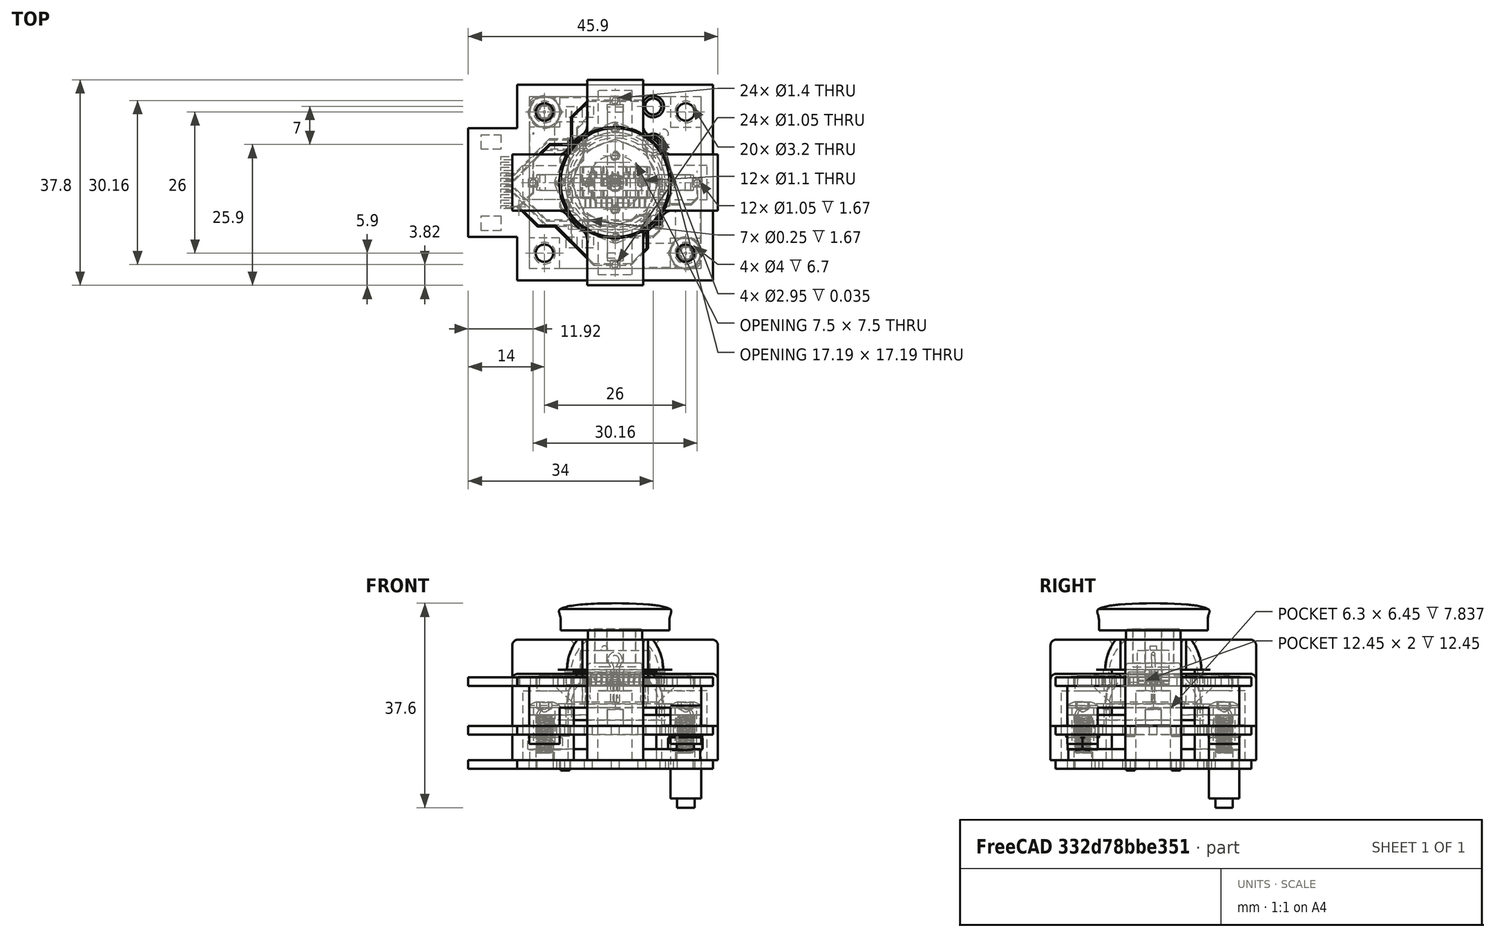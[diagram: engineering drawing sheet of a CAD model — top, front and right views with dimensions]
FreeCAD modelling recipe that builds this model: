
FCSTD DOCUMENT  (FreeCAD 0.21R33771 (Git))
Label: Thumbstick
License: All rights reserved
LicenseURL: http://en.wikipedia.org/wiki/All_rights_reserved
objects: Part::Feature×187, App::Part×27, PartDesign::Body×25, Sketcher::SketchObject×19, PartDesign::FeatureBase×16, PartDesign::ShapeBinder×14, PartDesign::Pad×12, App::DocumentObjectGroupPython×10, PartDesign::Fillet×9, Part::FeaturePython×6, PartDesign::Boolean×5, PartDesign::Pocket×4, PartDesign::SubShapeBinder×4, Mesh::Feature×4, PartDesign::Revolution×3, Spreadsheet::Sheet×1, PartDesign::Chamfer×1, App::DocumentObjectGroup×1
note: 334 computed .brp shape members not serialized (recipe doc carries the construction recipe); baked Part::Feature solids carry a one-line shape summary decoded from their .brp

FEATURE [Spreadsheet::Sheet] Spreadsheet  label="params"
  cells = A2='pcb_board_outline; B2(pcb_board_outline)=36; A3='pcb_mounting_distance; B3(pcb_mounting_distance)=26; A4='pcb_sw_array_len; B4(pcb_sw_array_len)=32.8; A6='sw_x; B6(sw_x)=12.8; A7='sw_y; B7(sw_y)=5.8; A8='sw_z; B8(sw_z)=6.5; A9='sw_to_button_top; B9(sw_to_button_top)=7.35; A10='sw_array_gap; B10(sw_array_gap)=7.2; A11='sw_button_width; B11(sw_button_width)=2.9; A13='post_center_width; B13(post_center_width)=6; A14='post_height; B14(post_height)=10.5; A15='post_tip_height; B15(post_tip_height)=2; A16='arm_height; B16(arm_height)=2; A18='mating_cross_width; B18(mating_cross_width)=7.5; A19='mating_cross_slot_width; B19(mating_cross_slot_width)=3; A20='mating_cross_slot_depth; B20(mating_cross_slot_depth)=7; A22='swivel_shell_thickness; B22(swivel_shell_thickness)=2; A23='ccover_shell_thickness; B23(ccover_shell_thickness)=2; A25='stick_fit_tolerance; B25(stick_fit_tolerance)=0; A26='stick_extrusion_height; B26(stick_extrusion_height)=6; A27='stick_cap_height; B27(stick_cap_height)=5; A29='collar_outer_rim_height; B29(collar_outer_rim_height)=8; A30='collar_inner_rim_height; B30(collar_inner_rim_height)=7; A31='collar_width; B31(collar_width)=8; A32='collar_center_spacing; B32(collar_center_spacing)=15; A34='pcb_thickness; B34(pcb_thickness)=1.6; A35='pcb_clip_extrude; B35(pcb_clip_extrude)=1; A36='pcb_clip_overlang_length; B36(pcb_clip_overlang_length)=2.5; A38='pcb_allign_holes; B38(pcb_allign_holes)=1.6; A39='pcb_mounting_holes; B39(pcb_mounting_holes)=3; A40='pcb_sw_pth; B40(pcb_sw_pth)=1.1; A42='pcb_cover_overhang; B42(pcb_cover_overhang)=0.9; A43='pcb_clip_thickness; B43(pcb_clip_thickness)=1.5; A45='insert_length; B45(insert_length)=5.7; A46='insert_hole_dia; B46(insert_hole_dia)=4; A47='insert_min_wall_thickness; B47(insert_min_wall_thickness)=1.6
FEATURE [Sketcher::SketchObject] Sketch  label="Sketch_Arms"
  FullyConstrained = true
  MapMode = 5
  Support = -> [XY_Plane001]
  expr: Constraints[14] = <<params>>.pcb_sw_array_len - 5
  expr: Constraints[18] = <<params>>.sw_button_width
  sketch-geometry (12):
    g0: LineSegment StartX=-13.9 StartY=1.45 StartZ=0 EndX=-13.9 EndY=-1.45 EndZ=0
    g1: LineSegment StartX=-13.9 StartY=-1.45 StartZ=0 EndX=-1.45 EndY=-1.45 EndZ=0
    g2: LineSegment StartX=-1.45 StartY=-13.9 StartZ=0 EndX=1.45 EndY=-13.9 EndZ=0
    g3: LineSegment StartX=13.9 StartY=-1.45 StartZ=0 EndX=13.9 EndY=1.45 EndZ=0
    g4: LineSegment StartX=13.9 StartY=1.45 StartZ=0 EndX=1.45 EndY=1.45 EndZ=0
    g5: LineSegment StartX=1.45 StartY=1.45 StartZ=0 EndX=1.45 EndY=13.9 EndZ=0
    g6: LineSegment StartX=1.45 StartY=13.9 StartZ=0 EndX=-1.45 EndY=13.9 EndZ=0
    g7: LineSegment StartX=-1.45 StartY=13.9 StartZ=0 EndX=-1.45 EndY=1.45 EndZ=0
    g8: LineSegment StartX=-1.45 StartY=1.45 StartZ=0 EndX=-13.9 EndY=1.45 EndZ=0
    g9: LineSegment StartX=1.45 StartY=-13.9 StartZ=0 EndX=1.45 EndY=-1.45 EndZ=0
    g10: LineSegment StartX=1.45 StartY=-1.45 StartZ=0 EndX=13.9 EndY=-1.45 EndZ=0
    g11: LineSegment StartX=-1.45 StartY=-1.45 StartZ=0 EndX=-1.45 EndY=-13.9 EndZ=0
  constraints (30):
    c: Coincident(g8,g0)
    c: Coincident(g0,g1)
    c: Horizontal(g1)
    c: Coincident(g11,g2)
    c: Coincident(g2,g9)
    c: Coincident(g10,g3)
    c: Coincident(g3,g4)
    c: Coincident(g5,g6)
    c: Coincident(g6,g7)
    c: Symmetric(g11,g2,g-2)
    c: Symmetric(g6,g5,g-2)
    c: Symmetric(g8,g0,g-1)
    c: Symmetric(g3,g10,g-1)
    c: Equal(g6,g0)
    c: DistanceY(g2,g5) = 27.8
    c: Symmetric(g3,g8,g-2)
    c: Symmetric(g5,g2,g-1)
    c: Equal(g5,g4)
    c: DistanceY(g3,g3) = 2.9
    c: Horizontal(g8)
    c: Vertical(g9)
    c: Vertical(g11)
    c: Coincident(g9,g10)
    c: Coincident(g1,g11)
    c: Coincident(g8,g7)
    c: Coincident(g5,g4)
    c: Horizontal(g4)
    c: Vertical(g5)
    c: Horizontal(g10)
    c: Vertical(g7)
FEATURE [Sketcher::SketchObject] Sketch001  label="Sketch_Center"
  FullyConstrained = true
  MapMode = 5
  Placement = pos=(0,0,0) rot=(1,0,0;1.5708rad)
  Support = -> [XZ_Plane002]
  expr: Constraints[10] = <<params>>.sw_array_gap + 1
  expr: Constraints[11] = Spreadsheet.post_height
  expr: Constraints[19] = <<params>>.post_tip_height
  expr: Constraints[9] = <<params>>.arm_height
  sketch-geometry (7):
    g0: LineSegment StartX=8.2 StartY=2 StartZ=0 EndX=8.2 EndY=0 EndZ=0
    g1: LineSegment StartX=8.2 StartY=0 StartZ=0 EndX=0 EndY=0 EndZ=0
    g2: ArcOfCircle CenterX=0 CenterY=2 CenterZ=0 NormalX=0 NormalY=0 NormalZ=1 AngleXU=0 Radius=8.2 StartAngle=0 EndAngle=0.915197
    g3: LineSegment StartX=4.999 StartY=8.5 StartZ=0 EndX=4.999 EndY=10.5 EndZ=0
    g4: LineSegment StartX=4.999 StartY=10.5 StartZ=0 EndX=0 EndY=10.5 EndZ=0
    g5: LineSegment StartX=0 StartY=10.5 StartZ=0 EndX=0 EndY=0 EndZ=0
    g6: LineSegment StartX=8.2 StartY=2 StartZ=0 EndX=0 EndY=2 EndZ=0
  constraints (20):
    c: PointOnObject(g0,g-1)
    c: Vertical(g0)
    c: Coincident(g1,g0)
    c: Coincident(g3,g2)
    c: Vertical(g3)
    c: Coincident(g4,g3)
    c: PointOnObject(g4,g-2)
    c: Horizontal(g4)
    c: Coincident(g5,g4)
    c: DistanceY(g0,g0) = 2
    c: DistanceX(g-1,g0) = 8.2
    c: DistanceY(g-1,g4) = 10.5
    c: Coincident(g1,g-1)
    c: Coincident(g5,g1)
    c: Coincident(g6,g0)
    c: PointOnObject(g6,g5)
    c: Horizontal(g6)
    c: Coincident(g0,g2)
    c: Coincident(g2,g6)
    c: DistanceY(g3,g3) = 2
FEATURE [PartDesign::Revolution] Revolution
  Angle = 360
  Axis = (0,-2e-16,1)
  Base = (0,0,0)
  Placement = pos=(0,0,0) rot=(1,0,0;1.5708rad)
  Profile = -> Sketch001
  ReferenceAxis = -> Sketch001 [V_Axis]
  Reversed = true
FEATURE [PartDesign::Pad] Pad  label="Pad_Arms"
  Direction = (0,0,1)
  Length = 2
  Length2 = 10
  Profile = -> Sketch
  ReferenceAxis = -> Sketch [N_Axis]
  Type = 0
  expr: Length = <<params>>.arm_height
FEATURE [PartDesign::Body] Body  label="Arms"
  Group = -> [Sketch,Pad]
  Origin = -> Origin001
  Tip = -> Pad
FEATURE [PartDesign::Boolean] Boolean
  BaseFeature = -> Revolution
  Group = -> [Body]
  Type = 0
FEATURE [PartDesign::ShapeBinder] ShapeBinder
  Placement = pos=(0,0,0) rot=(1,0,0;1.5708rad)
  Support = -> [Revolution]
  TraceSupport = false
FEATURE [Sketcher::SketchObject] Sketch002  label="Sketch_PocketMatingCross"
  FullyConstrained = true
  MapMode = 5
  Placement = pos=(0,2.3e-15,10.5) rot=(0,0,1;3.14159rad)
  Support = -> [ShapeBinder]
  expr: Constraints[32] = <<params>>.mating_cross_width
  expr: Constraints[33] = <<params>>.mating_cross_slot_width
  sketch-geometry (12):
    g0: LineSegment StartX=-3.75 StartY=1.5 StartZ=0 EndX=-1.5 EndY=1.5 EndZ=0
    g1: LineSegment StartX=-1.5 StartY=3.75 StartZ=0 EndX=-1.5 EndY=1.5 EndZ=0
    g2: LineSegment StartX=-1.5 StartY=3.75 StartZ=0 EndX=1.5 EndY=3.75 EndZ=0
    g3: LineSegment StartX=1.5 StartY=3.75 StartZ=0 EndX=1.5 EndY=1.5 EndZ=0
    g4: LineSegment StartX=1.5 StartY=1.5 StartZ=0 EndX=3.75 EndY=1.5 EndZ=0
    g5: LineSegment StartX=3.75 StartY=1.5 StartZ=0 EndX=3.75 EndY=-1.5 EndZ=0
    g6: LineSegment StartX=3.75 StartY=-1.5 StartZ=0 EndX=1.5 EndY=-1.5 EndZ=0
    g7: LineSegment StartX=1.5 StartY=-1.5 StartZ=0 EndX=1.5 EndY=-3.75 EndZ=0
    g8: LineSegment StartX=1.5 StartY=-3.75 StartZ=0 EndX=-1.5 EndY=-3.75 EndZ=0
    g9: LineSegment StartX=-1.5 StartY=-3.75 StartZ=0 EndX=-1.5 EndY=-1.5 EndZ=0
    g10: LineSegment StartX=-1.5 StartY=-1.5 StartZ=0 EndX=-3.75 EndY=-1.5 EndZ=0
    g11: LineSegment StartX=-3.75 StartY=-1.5 StartZ=0 EndX=-3.75 EndY=1.5 EndZ=0
  constraints (34):
    c: Horizontal(g0)
    c: Coincident(g1,g0)
    c: Vertical(g1)
    c: Coincident(g2,g1)
    c: Horizontal(g2)
    c: Coincident(g3,g2)
    c: Vertical(g3)
    c: Coincident(g4,g3)
    c: Horizontal(g4)
    c: Coincident(g5,g4)
    c: Vertical(g5)
    c: Coincident(g6,g5)
    c: Horizontal(g6)
    c: Coincident(g7,g6)
    c: Coincident(g8,g7)
    c: Horizontal(g8)
    c: Coincident(g9,g8)
    c: Vertical(g9)
    c: Coincident(g10,g9)
    c: Horizontal(g10)
    c: Coincident(g11,g10)
    c: Coincident(g11,g0)
    c: Vertical(g11)
    c: Equal(g11,g5)
    c: Equal(g5,g8)
    c: Equal(g8,g2)
    c: Equal(g3,g7)
    c: Equal(g4,g0)
    c: Equal(g4,g3)
    c: Symmetric(g9,g6,g-2)
    c: Symmetric(g3,g6,g-1)
    c: Vertical(g7)
    c: DistanceX(g0,g4) = 7.5
    c: DistanceX(g2,g2) = 3
FEATURE [PartDesign::Pocket] Pocket  label="Pocket_mating_cross"
  BaseFeature = -> Boolean
  Direction = (0,2e-16,-1)
  Length = 7
  Length2 = 5
  Profile = -> Sketch002
  ReferenceAxis = -> Sketch002 [N_Axis]
  Type = 0
  expr: Length = <<params>>.mating_cross_slot_depth
FEATURE [Part::Feature] Part__Feature  label="Fusion"
  shape: bbox 12.8 x 5.8 x 10.85 mm, 76 faces (baked)
FEATURE [App::Part] Kailh_GM_4_0
  Group = -> [Part__Feature]
  Origin = -> Origin005
  Placement = pos=(10,0,1.65) rot=(0,0,1;3.14159rad)
FEATURE [Part::Feature] Part__Feature001  label="Fusion001"
  shape: bbox 12.8 x 5.8 x 10.85 mm, 76 faces (baked)
FEATURE [App::Part] Kailh_GM_4_001
  Group = -> [Part__Feature001]
  Origin = -> Origin006
  Placement = pos=(0,10,1.65) rot=(0,0,-1;1.5708rad)
FEATURE [Part::Feature] Part__Feature002  label="C_0805_2012Metric"
  shape: bbox 2 x 1.25 x 1.25 mm, 28 faces (baked)
FEATURE [App::Part] C_0805_2012Metric  label="C_0805_2012Metric001"
  Group = -> [Part__Feature002]
  Origin = -> Origin007
  Placement = pos=(-7,7,1.65) rot=(0,0,1;0rad)
FEATURE [Part::Feature] Part__Feature003  label="C_0805_2012Metric002"
  shape: bbox 2 x 1.25 x 1.25 mm, 28 faces (baked)
FEATURE [App::Part] C_0805_2012Metric001  label="C_0805_2012Metric003"
  Group = -> [Part__Feature003]
  Origin = -> Origin008
  Placement = pos=(6.9625,-7,1.65) rot=(0,0,1;0rad)
FEATURE [Part::Feature] Part__Feature004  label="Fusion002"
  shape: bbox 12.8 x 5.8 x 10.85 mm, 76 faces (baked)
FEATURE [App::Part] Kailh_GM_4_002
  Group = -> [Part__Feature004]
  Origin = -> Origin009
  Placement = pos=(-10,0,1.65) rot=(0,0,1;0rad)
FEATURE [Part::Feature] Part__Feature005  label="Fusion003"
  shape: bbox 12.8 x 5.8 x 10.85 mm, 76 faces (baked)
FEATURE [App::Part] Kailh_GM_4_003
  Group = -> [Part__Feature005]
  Origin = -> Origin010
  Placement = pos=(0,-10,1.65) rot=(0,0,1;1.5708rad)
FEATURE [Part::Feature] Part__Feature006  label="TE_1_84952_0"
  shape: bbox 17.92 x 6.54 x 2.56 mm, 212 faces (baked)
FEATURE [App::Part] TE_1_84952_0_1x10_1MP_P1_0mm_Horizontal  label="TE_1-84952-0_1x10-1MP_P1.0mm_Horizontal"
  Group = -> [Part__Feature006]
  Origin = -> Origin011
  Placement = pos=(-21.8,0,-0.05) rot=(0.707107,0.707107,0;3.14159rad)
FEATURE [Part::Feature] Part__Feature007  label="SOT_23_6"
  shape: bbox 2.8 x 2.9 x 1.55 mm, 124 faces (baked)
FEATURE [App::Part] SOT_23_6  label="SOT-23-6"
  Group = -> [Part__Feature007]
  Origin = -> Origin012
  Placement = pos=(-7,7,-0.05) rot=(0,1,0;3.14159rad)
FEATURE [Part::Feature] Part__Feature008  label="SOT_23_007"
  shape: bbox 2.8 x 2.9 x 1.55 mm, 124 faces (baked)
FEATURE [App::Part] SOT_23_007  label="SOT-23-007"
  Group = -> [Part__Feature008]
  Origin = -> Origin013
  Placement = pos=(6.9625,-7,-0.05) rot=(0,1,0;3.14159rad)
FEATURE [Part::Feature] Part__Feature009  label="thumbpad_track_1"
  shape: bbox 0.125 x 0.2 x 0.035 mm, 6 faces (baked)
FEATURE [Part::Feature] Part__Feature010  label="thumbpad_track_2"
  shape: bbox 0.25 x 0.25 x 0.035 mm, 6 faces (baked)
FEATURE [Part::Feature] Part__Feature011  label="thumbpad_track_3"
  shape: bbox 0.2 x 0.2 x 0.035 mm, 6 faces (baked)
FEATURE [Part::Feature] Part__Feature012  label="thumbpad_track_4"
  shape: bbox 6.2 x 0.2 x 0.035 mm, 6 faces (baked)
FEATURE [Part::Feature] Part__Feature013  label="thumbpad_track_5"
  shape: bbox 0.2 x 3.505 x 0.035 mm, 6 faces (baked)
FEATURE [Part::Feature] Part__Feature014  label="thumbpad_track_6"
  shape: bbox 4.505 x 0.2 x 0.035 mm, 6 faces (baked)
FEATURE [Part::Feature] Part__Feature015  label="thumbpad_track_7"
  shape: bbox 0.8002 x 0.8777 x 0.035 mm, 6 faces (baked)
FEATURE [Part::Feature] Part__Feature016  label="thumbpad_track_8"
  shape: bbox 0.2 x 1.442 x 0.035 mm, 7 faces (baked)
FEATURE [Part::Feature] Part__Feature017  label="thumbpad_track_9"
  shape: bbox 3.317 x 3.317 x 0.035 mm, 6 faces (baked)
FEATURE [Part::Feature] Part__Feature018  label="thumbpad_track_10"
  shape: bbox 2.505 x 0.2 x 0.035 mm, 6 faces (baked)
FEATURE [Part::Feature] Part__Feature019  label="thumbpad_track_11"
  shape: bbox 3.205 x 3.205 x 0.035 mm, 6 faces (baked)
FEATURE [Part::Feature] Part__Feature020  label="thumbpad_track_12"
  shape: bbox 1.28 x 1.28 x 0.035 mm, 6 faces (baked)
FEATURE [Part::Feature] Part__Feature021  label="thumbpad_track_13"
  shape: bbox 0.2 x 4.988 x 0.035 mm, 6 faces (baked)
FEATURE [Part::Feature] Part__Feature022  label="thumbpad_track_14"
  shape: bbox 3.988 x 0.2 x 0.035 mm, 6 faces (baked)
FEATURE [Part::Feature] Part__Feature023  label="thumbpad_track_15"
  shape: bbox 0.2 x 5.1 x 0.035 mm, 7 faces (baked)
FEATURE [Part::Feature] Part__Feature024  label="thumbpad_track_16"
  shape: bbox 7.28 x 7.28 x 0.035 mm, 6 faces (baked)
FEATURE [Part::Feature] Part__Feature025  label="thumbpad_track_17"
  shape: bbox 0.2 x 0.95 x 0.035 mm, 6 faces (baked)
FEATURE [Part::Feature] Part__Feature026  label="thumbpad_track_19"
  shape: bbox 3.622 x 3.622 x 0.035 mm, 7 faces (baked)
FEATURE [Part::Feature] Part__Feature027  label="thumbpad_track_20"
  shape: bbox 2.275 x 2.275 x 0.035 mm, 6 faces (baked)
FEATURE [Part::Feature] Part__Feature028  label="thumbpad_track_21"
  shape: bbox 0.2 x 2.505 x 0.035 mm, 7 faces (baked)
FEATURE [Part::Feature] Part__Feature029  label="thumbpad_track_22"
  shape: bbox 4.505 x 0.2 x 0.035 mm, 6 faces (baked)
FEATURE [Part::Feature] Part__Feature030  label="thumbpad_track_23"
  shape: bbox 3.505 x 0.2 x 0.035 mm, 6 faces (baked)
FEATURE [Part::Feature] Part__Feature031  label="thumbpad_track_24"
  shape: bbox 2.755 x 2.755 x 0.035 mm, 6 faces (baked)
FEATURE [Part::Feature] Part__Feature032  label="thumbpad_track_25"
  shape: bbox 3.413 x 0.2 x 0.035 mm, 6 faces (baked)
FEATURE [Part::Feature] Part__Feature033  label="thumbpad_track_26"
  shape: bbox 3.28 x 3.28 x 0.035 mm, 6 faces (baked)
FEATURE [Part::Feature] Part__Feature034  label="thumbpad_track_27"
  shape: bbox 2.314 x 0.2 x 0.035 mm, 6 faces (baked)
FEATURE [Part::Feature] Part__Feature035  label="thumbpad_track_28"
  shape: bbox 0.125 x 0.2 x 0.035 mm, 6 faces (baked)
FEATURE [Part::Feature] Part__Feature036  label="thumbpad_track_30"
  shape: bbox 0.2 x 1.85 x 0.035 mm, 7 faces (baked)
FEATURE [Part::Feature] Part__Feature037  label="thumbpad_track_31"
  shape: bbox 2.075 x 0.2 x 0.035 mm, 6 faces (baked)
FEATURE [Part::Feature] Part__Feature038  label="thumbpad_track_32"
  shape: bbox 6.7 x 6.7 x 0.035 mm, 6 faces (baked)
FEATURE [Part::Feature] Part__Feature039  label="thumbpad_track_33"
  shape: bbox 0.2 x 2.025 x 0.035 mm, 7 faces (baked)
FEATURE [Part::Feature] Part__Feature040  label="thumbpad_track_34"
  shape: bbox 8.025 x 0.2 x 0.035 mm, 6 faces (baked)
FEATURE [Part::Feature] Part__Feature041  label="thumbpad_track_35"
  shape: bbox 1.105 x 0.2 x 0.035 mm, 6 faces (baked)
FEATURE [Part::Feature] Part__Feature042  label="thumbpad_track_36"
  shape: bbox 1.15 x 1.15 x 0.035 mm, 6 faces (baked)
FEATURE [Part::Feature] Part__Feature043  label="thumbpad_track_37"
  shape: bbox 7.62 x 0.2 x 0.035 mm, 6 faces (baked)
FEATURE [Part::Feature] Part__Feature044  label="thumbpad_track_38"
  shape: bbox 6.65 x 6.65 x 0.035 mm, 6 faces (baked)
FEATURE [Part::Feature] Part__Feature045  label="thumbpad_track_39"
  shape: bbox 4.113 x 0.2 x 0.035 mm, 6 faces (baked)
FEATURE [Part::Feature] Part__Feature046  label="thumbpad_track_40"
  shape: bbox 1.7 x 0.2 x 0.035 mm, 6 faces (baked)
FEATURE [Part::Feature] Part__Feature047  label="thumbpad_track_41"
  shape: bbox 0.2 x 5.113 x 0.035 mm, 6 faces (baked)
FEATURE [Part::Feature] Part__Feature048  label="thumbpad_track_42"
  shape: bbox 0.3375 x 0.3375 x 0.035 mm, 6 faces (baked)
FEATURE [Part::Feature] Part__Feature049  label="thumbpad_track_43"
  shape: bbox 2.2 x 2.2 x 0.035 mm, 6 faces (baked)
FEATURE [Part::Feature] Part__Feature050  label="thumbpad_track_44"
  shape: bbox 1.7 x 0.2 x 0.035 mm, 6 faces (baked)
FEATURE [Part::Feature] Part__Feature051  label="thumbpad_track_45"
  shape: bbox 5.013 x 0.2 x 0.035 mm, 6 faces (baked)
FEATURE [Part::Feature] Part__Feature052  label="thumbpad_track_46"
  shape: bbox 5.75 x 5.75 x 0.035 mm, 6 faces (baked)
FEATURE [Part::Feature] Part__Feature053  label="thumbpad_track_47"
  shape: bbox 0.675 x 0.675 x 0.035 mm, 6 faces (baked)
FEATURE [Part::Feature] Part__Feature054  label="thumbpad_track_48"
  shape: bbox 0.2 x 1.2 x 0.035 mm, 6 faces (baked)
FEATURE [Part::Feature] Part__Feature055  label="thumbpad_track_49"
  shape: bbox 0.2 x 3.675 x 0.035 mm, 6 faces (baked)
FEATURE [Part::Feature] Part__Feature056  label="thumbpad_track_50"
  shape: bbox 0.8625 x 0.2 x 0.035 mm, 6 faces (baked)
FEATURE [Part::Feature] Part__Feature057  label="thumbpad_track_51"
  shape: bbox 4.845 x 0.2 x 0.035 mm, 6 faces (baked)
FEATURE [Part::Feature] Part__Feature058  label="thumbpad_track_52"
  shape: bbox 14.03 x 0.2 x 0.035 mm, 6 faces (baked)
FEATURE [Part::Feature] Part__Feature059  label="thumbpad_track_53"
  shape: bbox 1.105 x 0.2 x 0.035 mm, 6 faces (baked)
FEATURE [Part::Feature] Part__Feature060  label="thumbpad_track_54"
  shape: bbox 0.2 x 3.25 x 0.035 mm, 6 faces (baked)
FEATURE [Part::Feature] Part__Feature061  label="thumbpad_track_55"
  shape: bbox 6.65 x 6.65 x 0.035 mm, 6 faces (baked)
FEATURE [Part::Feature] Part__Feature062  label="thumbpad_track_56"
  shape: bbox 3.397 x 0.2 x 0.035 mm, 6 faces (baked)
FEATURE [Part::Feature] Part__Feature063  label="thumbpad_track_57"
  shape: bbox 2.25 x 2.25 x 0.035 mm, 6 faces (baked)
FEATURE [Part::Feature] Part__Feature064  label="thumbpad_track_58"
  shape: bbox 0.2 x 2.113 x 0.035 mm, 6 faces (baked)
FEATURE [Part::Feature] Part__Feature065  label="thumbpad_track_59"
  shape: bbox 3.944 x 3.944 x 0.035 mm, 6 faces (baked)
FEATURE [Part::Feature] Part__Feature066  label="thumbpad_track_60"
  shape: bbox 2.1 x 2.1 x 0.035 mm, 6 faces (baked)
FEATURE [Part::Feature] Part__Feature067  label="thumbpad_track_61"
  shape: bbox 0.2 x 3.735 x 0.035 mm, 7 faces (baked)
FEATURE [Part::Feature] Part__Feature068  label="thumbpad_track_62"
  shape: bbox 1.3 x 1.3 x 0.035 mm, 6 faces (baked)
FEATURE [Part::Feature] Part__Feature069  label="thumbpad_track_63"
  shape: bbox 0.2 x 1.15 x 0.035 mm, 6 faces (baked)
FEATURE [Part::Feature] Part__Feature070  label="thumbpad_track_64"
  shape: bbox 6.585 x 0.2 x 0.035 mm, 6 faces (baked)
FEATURE [Part::Feature] Part__Feature071  label="thumbpad_pad_5"
  shape: bbox 4 x 4 x 0.035 mm, 4 faces (baked)
FEATURE [Part::Feature] Part__Feature072  label="thumbpad_pad_6"
  shape: bbox 4 x 4 x 0.035 mm, 4 faces (baked)
FEATURE [Part::Feature] Part__Feature073  label="thumbpad_pad_7"
  shape: bbox 3 x 3 x 1.67 mm, 4 faces (baked)
FEATURE [Part::Feature] Part__Feature074  label="thumbpad_pad_8"
  shape: bbox 1.7 x 1.7 x 0.035 mm, 7 faces (baked)
FEATURE [Part::Feature] Part__Feature075  label="thumbpad_pad_9"
  shape: bbox 1.7 x 1.7 x 0.035 mm, 7 faces (baked)
FEATURE [Part::Feature] Part__Feature076  label="thumbpad_pad_10"
  shape: bbox 1.1 x 1.1 x 1.67 mm, 4 faces (baked)
FEATURE [Part::Feature] Part__Feature077  label="thumbpad_pad_11"
  shape: bbox 1.7 x 1.7 x 0.035 mm, 4 faces (baked)
FEATURE [Part::Feature] Part__Feature078  label="thumbpad_pad_12"
  shape: bbox 1.7 x 1.7 x 0.035 mm, 4 faces (baked)
FEATURE [Part::Feature] Part__Feature079  label="thumbpad_pad_13"
  shape: bbox 1.1 x 1.1 x 1.67 mm, 4 faces (baked)
FEATURE [Part::Feature] Part__Feature080  label="thumbpad_pad_14"
  shape: bbox 1.7 x 1.7 x 0.035 mm, 4 faces (baked)
FEATURE [Part::Feature] Part__Feature081  label="thumbpad_pad_15"
  shape: bbox 1.7 x 1.7 x 0.035 mm, 4 faces (baked)
FEATURE [Part::Feature] Part__Feature082  label="thumbpad_pad_16"
  shape: bbox 1.1 x 1.1 x 1.67 mm, 4 faces (baked)
FEATURE [Part::Feature] Part__Feature083  label="thumbpad_pad_19"
  shape: bbox 1.7 x 1.7 x 0.035 mm, 7 faces (baked)
FEATURE [Part::Feature] Part__Feature084  label="thumbpad_pad_20"
  shape: bbox 1.7 x 1.7 x 0.035 mm, 7 faces (baked)
FEATURE [Part::Feature] Part__Feature085  label="thumbpad_pad_21"
  shape: bbox 1.1 x 1.1 x 1.67 mm, 4 faces (baked)
FEATURE [Part::Feature] Part__Feature086  label="thumbpad_pad_22"
  shape: bbox 1.7 x 1.7 x 0.035 mm, 4 faces (baked)
FEATURE [Part::Feature] Part__Feature087  label="thumbpad_pad_23"
  shape: bbox 1.7 x 1.7 x 0.035 mm, 4 faces (baked)
FEATURE [Part::Feature] Part__Feature088  label="thumbpad_pad_24"
  shape: bbox 1.1 x 1.1 x 1.67 mm, 4 faces (baked)
FEATURE [Part::Feature] Part__Feature089  label="thumbpad_pad_25"
  shape: bbox 1.7 x 1.7 x 0.035 mm, 4 faces (baked)
FEATURE [Part::Feature] Part__Feature090  label="thumbpad_pad_26"
  shape: bbox 1.7 x 1.7 x 0.035 mm, 4 faces (baked)
FEATURE [Part::Feature] Part__Feature091  label="thumbpad_pad_27"
  shape: bbox 1.1 x 1.1 x 1.67 mm, 4 faces (baked)
FEATURE [Part::Feature] Part__Feature092  label="thumbpad_pad_28"
  shape: bbox 4 x 4 x 0.035 mm, 4 faces (baked)
FEATURE [Part::Feature] Part__Feature093  label="thumbpad_pad_29"
  shape: bbox 4 x 4 x 0.035 mm, 4 faces (baked)
FEATURE [Part::Feature] Part__Feature094  label="thumbpad_pad_30"
  shape: bbox 3 x 3 x 1.67 mm, 4 faces (baked)
FEATURE [Part::Feature] Part__Feature095  label="thumbpad_pad_31"
  shape: bbox 1.175 x 1.45 x 0.035 mm, 23 faces (baked)
FEATURE [Part::Feature] Part__Feature096  label="thumbpad_pad_32"
  shape: bbox 1.175 x 1.45 x 0.035 mm, 23 faces (baked)
FEATURE [Part::Feature] Part__Feature097  label="thumbpad_pad_33"
  shape: bbox 1.175 x 1.45 x 0.035 mm, 23 faces (baked)
FEATURE [Part::Feature] Part__Feature098  label="thumbpad_pad_34"
  shape: bbox 1.175 x 1.45 x 0.035 mm, 23 faces (baked)
FEATURE [Part::Feature] Part__Feature099  label="thumbpad_pad_37"
  shape: bbox 1.7 x 1.7 x 0.035 mm, 7 faces (baked)
FEATURE [Part::Feature] Part__Feature100  label="thumbpad_pad_38"
  shape: bbox 1.7 x 1.7 x 0.035 mm, 7 faces (baked)
FEATURE [Part::Feature] Part__Feature101  label="thumbpad_pad_39"
  shape: bbox 1.1 x 1.1 x 1.67 mm, 4 faces (baked)
FEATURE [Part::Feature] Part__Feature102  label="thumbpad_pad_40"
  shape: bbox 1.7 x 1.7 x 0.035 mm, 4 faces (baked)
FEATURE [Part::Feature] Part__Feature103  label="thumbpad_pad_41"
  shape: bbox 1.7 x 1.7 x 0.035 mm, 4 faces (baked)
FEATURE [Part::Feature] Part__Feature104  label="thumbpad_pad_42"
  shape: bbox 1.1 x 1.1 x 1.67 mm, 4 faces (baked)
FEATURE [Part::Feature] Part__Feature105  label="thumbpad_pad_43"
  shape: bbox 1.7 x 1.7 x 0.035 mm, 4 faces (baked)
FEATURE [Part::Feature] Part__Feature106  label="thumbpad_pad_44"
  shape: bbox 1.7 x 1.7 x 0.035 mm, 4 faces (baked)
FEATURE [Part::Feature] Part__Feature107  label="thumbpad_pad_45"
  shape: bbox 1.1 x 1.1 x 1.67 mm, 4 faces (baked)
FEATURE [Part::Feature] Part__Feature108  label="thumbpad_pad_46"
  shape: bbox 1.7 x 1.7 x 0.035 mm, 7 faces (baked)
FEATURE [Part::Feature] Part__Feature109  label="thumbpad_pad_47"
  shape: bbox 1.7 x 1.7 x 0.035 mm, 7 faces (baked)
FEATURE [Part::Feature] Part__Feature110  label="thumbpad_pad_48"
  shape: bbox 1.1 x 1.1 x 1.67 mm, 4 faces (baked)
FEATURE [Part::Feature] Part__Feature111  label="thumbpad_pad_49"
  shape: bbox 1.7 x 1.7 x 0.035 mm, 4 faces (baked)
FEATURE [Part::Feature] Part__Feature112  label="thumbpad_pad_50"
  shape: bbox 1.7 x 1.7 x 0.035 mm, 4 faces (baked)
FEATURE [Part::Feature] Part__Feature113  label="thumbpad_pad_51"
  shape: bbox 1.1 x 1.1 x 1.67 mm, 4 faces (baked)
FEATURE [Part::Feature] Part__Feature114  label="thumbpad_pad_52"
  shape: bbox 1.7 x 1.7 x 0.035 mm, 4 faces (baked)
FEATURE [Part::Feature] Part__Feature115  label="thumbpad_pad_53"
  shape: bbox 1.7 x 1.7 x 0.035 mm, 4 faces (baked)
FEATURE [Part::Feature] Part__Feature116  label="thumbpad_pad_54"
  shape: bbox 1.1 x 1.1 x 1.67 mm, 4 faces (baked)
FEATURE [Part::Feature] Part__Feature117  label="thumbpad_pad_55"
  shape: bbox 2 x 2 x 0.035 mm, 6 faces (baked)
FEATURE [Part::Feature] Part__Feature118  label="thumbpad_pad_56"
  shape: bbox 2 x 2 x 0.035 mm, 6 faces (baked)
FEATURE [Part::Feature] Part__Feature119  label="thumbpad_pad_57"
  shape: bbox 2 x 0.61 x 0.035 mm, 6 faces (baked)
FEATURE [Part::Feature] Part__Feature120  label="thumbpad_pad_58"
  shape: bbox 2 x 0.61 x 0.035 mm, 6 faces (baked)
FEATURE [Part::Feature] Part__Feature121  label="thumbpad_pad_59"
  shape: bbox 2 x 0.61 x 0.035 mm, 6 faces (baked)
FEATURE [Part::Feature] Part__Feature122  label="thumbpad_pad_60"
  shape: bbox 2 x 0.61 x 0.035 mm, 6 faces (baked)
FEATURE [Part::Feature] Part__Feature123  label="thumbpad_pad_61"
  shape: bbox 2 x 0.61 x 0.035 mm, 6 faces (baked)
FEATURE [Part::Feature] Part__Feature124  label="thumbpad_pad_62"
  shape: bbox 2 x 0.61 x 0.035 mm, 6 faces (baked)
FEATURE [Part::Feature] Part__Feature125  label="thumbpad_pad_63"
  shape: bbox 2 x 0.61 x 0.035 mm, 6 faces (baked)
FEATURE [Part::Feature] Part__Feature126  label="thumbpad_pad_64"
  shape: bbox 2 x 0.61 x 0.035 mm, 6 faces (baked)
FEATURE [Part::Feature] Part__Feature127  label="thumbpad_pad_65"
  shape: bbox 2 x 0.61 x 0.035 mm, 6 faces (baked)
FEATURE [Part::Feature] Part__Feature128  label="thumbpad_pad_66"
  shape: bbox 2 x 0.61 x 0.035 mm, 6 faces (baked)
FEATURE [Part::Feature] Part__Feature129  label="thumbpad_pad_67"
  shape: bbox 3.6 x 2.68 x 0.035 mm, 6 faces (baked)
FEATURE [Part::Feature] Part__Feature130  label="thumbpad_pad_68"
  shape: bbox 3.6 x 2.68 x 0.035 mm, 6 faces (baked)
FEATURE [Part::Feature] Part__Feature131  label="thumbpad_pad_69"
  shape: bbox 1.325 x 0.6 x 0.035 mm, 22 faces (baked)
FEATURE [Part::Feature] Part__Feature132  label="thumbpad_pad_70"
  shape: bbox 1.325 x 0.6 x 0.035 mm, 23 faces (baked)
FEATURE [Part::Feature] Part__Feature133  label="thumbpad_pad_71"
  shape: bbox 1.325 x 0.6 x 0.035 mm, 22 faces (baked)
FEATURE [Part::Feature] Part__Feature134  label="thumbpad_pad_72"
  shape: bbox 1.325 x 0.6 x 0.035 mm, 22 faces (baked)
FEATURE [Part::Feature] Part__Feature135  label="thumbpad_pad_73"
  shape: bbox 1.325 x 0.6 x 0.035 mm, 23 faces (baked)
FEATURE [Part::Feature] Part__Feature136  label="thumbpad_pad_74"
  shape: bbox 1.325 x 0.6 x 0.035 mm, 22 faces (baked)
FEATURE [Part::Feature] Part__Feature137  label="thumbpad_pad_75"
  shape: bbox 2 x 2 x 0.035 mm, 6 faces (baked)
FEATURE [Part::Feature] Part__Feature138  label="thumbpad_pad_76"
  shape: bbox 1.325 x 0.6 x 0.035 mm, 22 faces (baked)
FEATURE [Part::Feature] Part__Feature139  label="thumbpad_pad_77"
  shape: bbox 1.325 x 0.6 x 0.035 mm, 23 faces (baked)
FEATURE [Part::Feature] Part__Feature140  label="thumbpad_pad_78"
  shape: bbox 1.325 x 0.6 x 0.035 mm, 22 faces (baked)
FEATURE [Part::Feature] Part__Feature141  label="thumbpad_pad_79"
  shape: bbox 1.325 x 0.6 x 0.035 mm, 22 faces (baked)
FEATURE [Part::Feature] Part__Feature142  label="thumbpad_pad_80"
  shape: bbox 1.325 x 0.6 x 0.035 mm, 23 faces (baked)
FEATURE [Part::Feature] Part__Feature143  label="thumbpad_pad_81"
  shape: bbox 1.325 x 0.6 x 0.035 mm, 22 faces (baked)
FEATURE [Part::Feature] Part__Feature144  label="thumbpad_pad_82"
  shape: bbox 2 x 2 x 0.035 mm, 6 faces (baked)
FEATURE [Part::Feature] Part__Feature145  label="thumbpad_pad_83"
  shape: bbox 0.6 x 0.6 x 0.035 mm, 4 faces (baked)
FEATURE [Part::Feature] Part__Feature146  label="thumbpad_pad_84"
  shape: bbox 0.6 x 0.6 x 0.035 mm, 4 faces (baked)
FEATURE [Part::Feature] Part__Feature147  label="thumbpad_pad_85"
  shape: bbox 0.3 x 0.3 x 1.67 mm, 4 faces (baked)
FEATURE [Part::Feature] Part__Feature148  label="thumbpad_pad_86"
  shape: bbox 0.6 x 0.6 x 0.035 mm, 4 faces (baked)
FEATURE [Part::Feature] Part__Feature149  label="thumbpad_pad_87"
  shape: bbox 0.6 x 0.6 x 0.035 mm, 4 faces (baked)
FEATURE [Part::Feature] Part__Feature150  label="thumbpad_pad_88"
  shape: bbox 0.3 x 0.3 x 1.67 mm, 4 faces (baked)
FEATURE [Part::Feature] Part__Feature151  label="thumbpad_pad_89"
  shape: bbox 0.6 x 0.6 x 0.035 mm, 4 faces (baked)
FEATURE [Part::Feature] Part__Feature152  label="thumbpad_pad_90"
  shape: bbox 0.6 x 0.6 x 0.035 mm, 4 faces (baked)
FEATURE [Part::Feature] Part__Feature153  label="thumbpad_pad_91"
  shape: bbox 0.3 x 0.3 x 1.67 mm, 4 faces (baked)
FEATURE [Part::Feature] Part__Feature154  label="thumbpad_pad_92"
  shape: bbox 0.6 x 0.6 x 0.035 mm, 4 faces (baked)
FEATURE [Part::Feature] Part__Feature155  label="thumbpad_pad_93"
  shape: bbox 0.6 x 0.6 x 0.035 mm, 4 faces (baked)
FEATURE [Part::Feature] Part__Feature156  label="thumbpad_pad_94"
  shape: bbox 0.3 x 0.3 x 1.67 mm, 4 faces (baked)
FEATURE [Part::Feature] Part__Feature157  label="thumbpad_pad_95"
  shape: bbox 0.6 x 0.6 x 0.035 mm, 4 faces (baked)
FEATURE [Part::Feature] Part__Feature158  label="thumbpad_pad_96"
  shape: bbox 0.6 x 0.6 x 0.035 mm, 4 faces (baked)
FEATURE [Part::Feature] Part__Feature159  label="thumbpad_pad_97"
  shape: bbox 0.3 x 0.3 x 1.67 mm, 4 faces (baked)
FEATURE [Part::Feature] Part__Feature160  label="thumbpad_pad_98"
  shape: bbox 0.6 x 0.6 x 0.035 mm, 4 faces (baked)
FEATURE [Part::Feature] Part__Feature161  label="thumbpad_pad_99"
  shape: bbox 0.6 x 0.6 x 0.035 mm, 4 faces (baked)
FEATURE [Part::Feature] Part__Feature162  label="thumbpad_pad_100"
  shape: bbox 0.3 x 0.3 x 1.67 mm, 4 faces (baked)
FEATURE [Part::Feature] Part__Feature163  label="thumbpad_pad_101"
  shape: bbox 0.6 x 0.6 x 0.035 mm, 4 faces (baked)
FEATURE [Part::Feature] Part__Feature164  label="thumbpad_pad_102"
  shape: bbox 0.6 x 0.6 x 0.035 mm, 4 faces (baked)
FEATURE [Part::Feature] Part__Feature165  label="thumbpad_pad_103"
  shape: bbox 0.3 x 0.3 x 1.67 mm, 4 faces (baked)
FEATURE [Part::Feature] Part__Feature166  label="thumbpad_PCB"
  shape: bbox 45 x 36 x 1.6 mm, 35 faces (baked)
FEATURE [App::Part] thumbpad_1  label="thumbpad_pcb"
  Group = -> [Kailh_GM_4_0,Kailh_GM_4_001,C_0805_2012Metric,C_0805_2012Metric001,Kailh_GM_4_002,Kailh_GM_4_003,TE_1_84952_0_1x10_1MP_P1_0mm_Horizontal,SOT_23_6,SOT_23_007,Part__Feature009,Part__Feature010,Part__Feature011,Part__Feature012,Part__Feature013,Part__Feature014,Part__Feature015,Part__Feature016,Part__Feature017,Part__Feature018,Part__Feature019,Part__Feature020,Part__Feature021,Part__Feature022,+144 more]
  Origin = -> Origin014
  Placement = pos=(0,0,-9) rot=(0,0,1;0rad)
FEATURE [PartDesign::SubShapeBinder] Binder002  label="Binder_MatingCross_surface"
  BindCopyOnChange = 0
  BindMode = 0
  ClaimChildren = false
  Context = -> Part002 [Body003.Binder002.]
  Fuse = false
  MakeFace = true
  OffsetFill = false
  OffsetIntersection = false
  OffsetJoinType = 0
  OffsetOpenResult = false
  PartialLoad = false
  Relative = true
  Support = -> [Part[Body001.Pocket.Face45]]
  _Version = 2
FEATURE [Part::Feature] Part__Feature167  label="Fusion004"
  shape: bbox 12.8 x 5.8 x 10.85 mm, 76 faces (baked)
FEATURE [App::Part] Kailh_GM_4_004
  Group = -> [Part__Feature167]
  Origin = -> Origin024
  Placement = pos=(10,0,1.65) rot=(0,0,1;3.14159rad)
FEATURE [Part::Feature] Part__Feature168  label="Fusion005"
  shape: bbox 12.8 x 5.8 x 10.85 mm, 76 faces (baked)
FEATURE [App::Part] Kailh_GM_4_005
  Group = -> [Part__Feature168]
  Origin = -> Origin025
  Placement = pos=(0,10,1.65) rot=(0,0,-1;1.5708rad)
FEATURE [Part::Feature] Part__Feature171  label="C_0805_2012Metric006"
  shape: bbox 2 x 1.25 x 1.25 mm, 28 faces (baked)
FEATURE [App::Part] C_0805_2012Metric003  label="C_0805_2012Metric007"
  Group = -> [Part__Feature171]
  Origin = -> Origin028
  Placement = pos=(6.9625,-7,1.65) rot=(0,0,1;0rad)
FEATURE [Part::Feature] Part__Feature172  label="Fusion006"
  shape: bbox 12.8 x 5.8 x 10.85 mm, 76 faces (baked)
FEATURE [App::Part] Kailh_GM_4_006
  Group = -> [Part__Feature172]
  Origin = -> Origin029
  Placement = pos=(-10,0,1.65) rot=(0,0,1;0rad)
FEATURE [Part::Feature] Part__Feature173  label="Fusion007"
  shape: bbox 12.8 x 5.8 x 10.85 mm, 76 faces (baked)
FEATURE [App::Part] Kailh_GM_4_007
  Group = -> [Part__Feature173]
  Origin = -> Origin030
  Placement = pos=(0,-10,1.65) rot=(0,0,1;1.5708rad)
FEATURE [Part::Feature] Part__Feature176  label="SOT_23_009"
  shape: bbox 2.8 x 2.9 x 1.55 mm, 124 faces (baked)
FEATURE [App::Part] SOT_23_009  label="SOT-23-009"
  Group = -> [Part__Feature176]
  Origin = -> Origin033
  Placement = pos=(6.9625,-7,-0.05) rot=(0,1,0;3.14159rad)
FEATURE [Part::Feature] Part__Feature175  label="SOT_23_008"
  shape: bbox 2.8 x 2.9 x 1.55 mm, 124 faces (baked)
FEATURE [App::Part] SOT_23_008  label="SOT-23-008"
  Group = -> [Part__Feature175]
  Origin = -> Origin032
  Placement = pos=(-7,9,-0.05) rot=(0,1,0;3.14159rad)
FEATURE [Part::Feature] Part__Feature174  label="TE_1_84952_001"
  shape: bbox 17.92 x 6.54 x 2.56 mm, 212 faces (baked)
FEATURE [App::Part] TE_1_84952_0_1x10_1MP_P1_0mm_Horizontal001  label="TE_1-84952-0_1x10-1MP_P1.0mm_Horizontal001"
  Group = -> [Part__Feature174]
  Origin = -> Origin031
  Placement = pos=(-21.8,0,-0.05) rot=(0.707107,0.707107,0;3.14159rad)
FEATURE [Part::Feature] Part__Feature169  label="TestPoint_Loop_D2_60mm_Drill1_6mm_Beaded_cp"
  shape: bbox 3.649 x 3.2 x 9.307 mm, 11 faces, 2 solids (baked)
FEATURE [App::Part] TestPoint_Loop_D2_60mm_Drill1_6mm_Beaded  label="TestPoint_Loop_D2.60mm_Drill1.6mm_Beaded"
  Group = -> [Part__Feature169]
  Origin = -> Origin026
  Placement = pos=(9,9,1.65) rot=(0,0,1;0rad)
FEATURE [Part::Feature] Part__Feature170  label="C_0805_2012Metric004"
  shape: bbox 2 x 1.25 x 1.25 mm, 28 faces (baked)
FEATURE [App::Part] C_0805_2012Metric002  label="C_0805_2012Metric005"
  Group = -> [Part__Feature170]
  Origin = -> Origin027
  Placement = pos=(-7,9,1.65) rot=(0,0,1;0rad)
FEATURE [Part::Feature] Part__Feature177  label="thumbpad_PCB001"
  shape: bbox 45 x 36 x 1.6 mm, 29 faces (baked)
FEATURE [PartDesign::FeatureBase] BaseFeature
  BaseFeature = -> Part__Feature177
FEATURE [PartDesign::ShapeBinder] ShapeBinder010
  Support = -> [BaseFeature]
  TraceSupport = false
FEATURE [Sketcher::SketchObject] Sketch016
  ExternalGeometry = -> [BaseFeature]
  FullyConstrained = true
  MapMode = 5
  Placement = pos=(0,0,1.6) rot=(0,0,1;0rad)
  Support = -> [ShapeBinder010]
  expr: Constraints[8] = <<params>>.pcb_sw_pth + 0.3
  expr: Constraints[9] = <<params>>.pcb_allign_holes + 0.4
  sketch-geometry (14):
    g0: Circle CenterX=-15.08 CenterY=0 CenterZ=0 NormalX=0 NormalY=0 NormalZ=1 AngleXU=0 Radius=0.7
    g1: Circle CenterX=-10 CenterY=0 CenterZ=0 NormalX=0 NormalY=0 NormalZ=1 AngleXU=0 Radius=0.7
    g2: Circle CenterX=-4.92 CenterY=0 CenterZ=0 NormalX=0 NormalY=0 NormalZ=1 AngleXU=0 Radius=0.7
    g3: Circle CenterX=-9.23 CenterY=-4.15 CenterZ=0 NormalX=0 NormalY=0 NormalZ=1 AngleXU=0 Radius=1
    g4: Circle CenterX=-9.23 CenterY=4.15 CenterZ=0 NormalX=0 NormalY=0 NormalZ=1 AngleXU=0 Radius=1
    g5: Circle CenterX=0 CenterY=-4.92 CenterZ=0 NormalX=0 NormalY=0 NormalZ=1 AngleXU=0 Radius=0.7
    g6: Circle CenterX=0 CenterY=-10 CenterZ=0 NormalX=0 NormalY=0 NormalZ=1 AngleXU=0 Radius=0.7
    g7: Circle CenterX=0 CenterY=-15.08 CenterZ=0 NormalX=0 NormalY=0 NormalZ=1 AngleXU=0 Radius=0.7
    g8: Circle CenterX=4.92 CenterY=0 CenterZ=0 NormalX=0 NormalY=0 NormalZ=1 AngleXU=0 Radius=0.7
    g9: Circle CenterX=10 CenterY=0 CenterZ=0 NormalX=0 NormalY=0 NormalZ=1 AngleXU=0 Radius=0.7
    g10: Circle CenterX=15.08 CenterY=0 CenterZ=0 NormalX=0 NormalY=0 NormalZ=1 AngleXU=0 Radius=0.7
    g11: Circle CenterX=0 CenterY=4.92 CenterZ=0 NormalX=0 NormalY=0 NormalZ=1 AngleXU=0 Radius=0.7
    g12: Circle CenterX=0 CenterY=10 CenterZ=0 NormalX=0 NormalY=0 NormalZ=1 AngleXU=0 Radius=0.7
    g13: Circle CenterX=0 CenterY=15.08 CenterZ=0 NormalX=0 NormalY=0 NormalZ=1 AngleXU=0 Radius=0.7
  constraints (28):
    c: Coincident(g0,g-5)
    c: Coincident(g1,g-4)
    c: Coincident(g2,g-3)
    c: Coincident(g3,g-7)
    c: Coincident(g4,g-6)
    c: Equal(g0,g1)
    c: Equal(g1,g2)
    c: Equal(g3,g4)
    c: Diameter(g1) = 1.4
    c: Diameter(g4) = 2
    c: Coincident(g5,g-8)
    c: Coincident(g6,g-9)
    c: Coincident(g7,g-13)
    c: Coincident(g8,g-10)
    c: Coincident(g9,g-11)
    c: Coincident(g10,g-12)
    c: Coincident(g11,g-14)
    c: Coincident(g12,g-15)
    c: Equal(g12,g11)
    c: Equal(g11,g5)
    c: Equal(g5,g8)
    c: Equal(g8,g9)
    c: Equal(g9,g10)
    c: Equal(g10,g6)
    c: Equal(g6,g7)
    c: Equal(g7,g1)
    c: Coincident(g13,g-16)
    c: Equal(g12,g13)
FEATURE [PartDesign::Pocket] Pocket002
  BaseFeature = -> BaseFeature
  Direction = (0,0,-1)
  Length = 5
  Length2 = 5
  Profile = -> Sketch016
  ReferenceAxis = -> Sketch016 [N_Axis]
  Type = 0
FEATURE [PartDesign::Body] Body010  label="HoleEnlarge"
  BaseFeature = -> Part__Feature177
  Group = -> [BaseFeature,ShapeBinder010,Sketch016,Pocket002]
  Origin = -> Origin035
  Tip = -> Pocket002
FEATURE [App::Part] thumbpad_002  label="thumbpad_PCB_3DPrintEdit"
  Group = -> [Kailh_GM_4_004,Kailh_GM_4_005,TestPoint_Loop_D2_60mm_Drill1_6mm_Beaded,C_0805_2012Metric002,C_0805_2012Metric003,Kailh_GM_4_006,Kailh_GM_4_007,TE_1_84952_0_1x10_1MP_P1_0mm_Horizontal001,SOT_23_008,SOT_23_009,Body010]
  Origin = -> Origin034
  Placement = pos=(0,0,-9) rot=(0,0,1;0rad)
FEATURE [PartDesign::Fillet] Fillet004
  Base = -> Pocket [Edge43,Edge34,Edge52,Edge59]
  BaseFeature = -> Pocket
  Radius = 1
  SupportTransform = false
  UseAllEdges = false
FEATURE [PartDesign::Fillet] Fillet005
  Base = -> Fillet004 [Edge44]
  BaseFeature = -> Fillet004
  Radius = 0.5
  SupportTransform = false
  UseAllEdges = false
FEATURE [PartDesign::Body] Body001  label="Rotation_Center_Ball"
  Group = -> [Sketch001,Revolution,Boolean,ShapeBinder,Sketch002,Pocket,Fillet004,Fillet005]
  Origin = -> Origin002
  Tip = -> Fillet005
FEATURE [App::Part] Part  label="BaseContactSwivel"
  Group = -> [Body001]
  Origin = -> Origin
FEATURE [Part::FeaturePython] Screw  label="M3x7-Screw"  # Fasteners workbench fastener (typed FeaturePython)
  Placement = pos=(13,-13,-5.35) rot=(0,0,1;0rad)
  diameter = 3
  invert = false
  leftHanded = false
  length = 11
  lengthCustom = 7
  matchOuter = false
  offset = 0
  thread = true
  type = 56
FEATURE [Part::FeaturePython] Washer  label="M3-Washer"  # Fasteners workbench fastener (typed FeaturePython)
  Placement = pos=(13,-13,-9.5) rot=(0,0,1;0rad)
  diameter = 4
  invert = false
  matchOuter = false
  offset = 0
  type = 10
FEATURE [Part::FeaturePython] Nut  label="M3-Nut"  # Fasteners workbench fastener (typed FeaturePython)
  Placement = pos=(12.9,-13,-11.8) rot=(0,0,1;0rad)
  diameter = 4
  invert = false
  leftHanded = false
  matchOuter = false
  offset = 0
  thread = false
  type = 31
FEATURE [Part::FeaturePython] Screw001  label="M3x7-Screw001"  # Fasteners workbench fastener (typed FeaturePython)
  Placement = pos=(-13,13,-5.35) rot=(0,0,1;0rad)
  diameter = 3
  invert = false
  leftHanded = false
  length = 11
  lengthCustom = 7
  matchOuter = false
  offset = 0
  thread = true
  type = 56
FEATURE [Part::FeaturePython] Washer001  label="M3-Washer001"  # Fasteners workbench fastener (typed FeaturePython)
  Placement = pos=(-13,13,-9.5) rot=(0,0,1;0rad)
  diameter = 4
  invert = false
  matchOuter = false
  offset = 0
  type = 10
FEATURE [Part::FeaturePython] Nut001  label="M3-Nut001"  # Fasteners workbench fastener (typed FeaturePython)
  Placement = pos=(-12.9,13,-11.8) rot=(0,0,1;0rad)
  diameter = 4
  invert = false
  leftHanded = false
  matchOuter = false
  offset = 0
  thread = false
  type = 31
FEATURE [Sketcher::SketchObject] Sketch003  label="Sketch_ShellRevolution"
  FullyConstrained = true
  MapMode = 5
  Placement = pos=(0,0,0) rot=(1,0,0;1.5708rad)
  expr: Constraints[10] = <<params>>.arm_height + 1
  expr: Constraints[14] = <<params>>.sw_array_gap + 1.5
  expr: Constraints[15] = <<params>>.swivel_shell_thickness
  expr: Constraints[23] = Spreadsheet.post_height
  expr: Constraints[24] = <<params>>.post_tip_height
  sketch-geometry (9):
    g0: ArcOfCircle CenterX=0 CenterY=3 CenterZ=0 NormalX=0 NormalY=0 NormalZ=1 AngleXU=0 Radius=8.7 StartAngle=0 EndAngle=0.684369
    g1: LineSegment StartX=6.74092 StartY=8.5 StartZ=0 EndX=9.17824 EndY=8.5 EndZ=0
    g2: LineSegment StartX=8.7 StartY=3 StartZ=0 EndX=10.7 EndY=3 EndZ=0
    g3: ArcOfCircle CenterX=0 CenterY=3 CenterZ=0 NormalX=0 NormalY=0 NormalZ=1 AngleXU=0 Radius=10.7 StartAngle=0 EndAngle=0.539863
    g4: LineSegment StartX=0 StartY=0 StartZ=0 EndX=0 EndY=3 EndZ=0
    g5: LineSegment StartX=0 StartY=3 StartZ=0 EndX=8.7 EndY=3 EndZ=0
    g6: LineSegment StartX=0 StartY=3 StartZ=0 EndX=0 EndY=8.5 EndZ=0
    g7: LineSegment StartX=0 StartY=8.5 StartZ=0 EndX=0 EndY=10.5 EndZ=0
    g8: LineSegment StartX=0 StartY=8.5 StartZ=0 EndX=6.74092 EndY=8.5 EndZ=0
  constraints (25):
    c: PointOnObject(g0,g-2)
    c: Coincident(g1,g0)
    c: Horizontal(g1)
    c: Coincident(g2,g0)
    c: Horizontal(g2)
    c: Coincident(g3,g0)
    c: Coincident(g3,g2)
    c: Coincident(g3,g1)
    c: Coincident(g4,g-1)
    c: Coincident(g4,g0)
    c: DistanceY(g4,g4) = 3
    c: Coincident(g5,g0)
    c: Coincident(g5,g0)
    c: Horizontal(g5)
    c: DistanceX(g5,g5) = 8.7
    c: DistanceX(g2,g2) = 2
    c: Coincident(g6,g0)
    c: PointOnObject(g6,g-2)
    c: PointOnObject(g7,g-2)
    c: Coincident(g8,g7)
    c: Coincident(g8,g0)
    c: Horizontal(g8)
    c: Coincident(g6,g8)
    c: DistanceY(g4,g7) = 10.5
    c: DistanceY(g7,g7) = 2
FEATURE [PartDesign::Revolution] Revolution001  label="Revolution_Shell"
  Angle = 360
  Axis = (0,2e-16,1)
  Base = (0,0,0)
  Placement = pos=(0,0,0) rot=(1,0,0;1.5708rad)
  Profile = -> Sketch003
  ReferenceAxis = -> Sketch003 [V_Axis]
  Reversed = true
FEATURE [PartDesign::SubShapeBinder] Binder001  label="Binder_ShellTop"
  BindCopyOnChange = 0
  BindMode = 0
  ClaimChildren = false
  Context = -> Part001 [Body015.Binder001.]
  Fuse = false
  MakeFace = true
  OffsetFill = false
  OffsetIntersection = false
  OffsetJoinType = 0
  OffsetOpenResult = false
  PartialLoad = false
  Relative = true
  Support = -> [Revolution001[Face2]]
  _Version = 2
FEATURE [PartDesign::ShapeBinder] ShapeBinder001  label="ShapeBinder_ShellBottom"
  Placement = pos=(0,0,0) rot=(1,0,0;1.5708rad)
  Support = -> [Revolution001]
  TraceSupport = true
FEATURE [Sketcher::SketchObject] Sketch004  label="Sketch_ContactCovers"
  ExternalGeometry = -> [Binder001,Revolution001]
  FullyConstrained = true
  MapMode = 5
  Placement = pos=(0,1e-15,3) rot=(1,0,0;3.14159rad)
  Support = -> [ShapeBinder001]
  expr: Constraints[30] = <<params>>.sw_y + <<params>>.ccover_shell_thickness * 2 + 0.5
  expr: Constraints[31] = <<params>>.sw_array_gap / 2 + <<params>>.sw_x + <<params>>.ccover_shell_thickness + 0.5
  sketch-geometry (16):
    g0: LineSegment StartX=5.15 StartY=-7.5972 StartZ=0 EndX=5.15 EndY=-18.9 EndZ=0
    g1: LineSegment StartX=5.15 StartY=-18.9 StartZ=0 EndX=-5.15 EndY=-18.9 EndZ=0
    g2: LineSegment StartX=-5.15 StartY=-18.9 StartZ=0 EndX=-5.15 EndY=-7.5972 EndZ=0
    g3: LineSegment StartX=-7.5972 StartY=-5.15 StartZ=0 EndX=-18.9 EndY=-5.15 EndZ=0
    g4: LineSegment StartX=-18.9 StartY=-5.15 StartZ=0 EndX=-18.9 EndY=5.15 EndZ=0
    g5: LineSegment StartX=-18.9 StartY=5.15 StartZ=0 EndX=-7.5972 EndY=5.15 EndZ=0
    g6: LineSegment StartX=7.5972 StartY=-5.15 StartZ=0 EndX=18.9 EndY=-5.15 EndZ=0
    g7: LineSegment StartX=18.9 StartY=-5.15 StartZ=0 EndX=18.9 EndY=5.15 EndZ=0
    g8: LineSegment StartX=18.9 StartY=5.15 StartZ=0 EndX=7.5972 EndY=5.15 EndZ=0
    g9: LineSegment StartX=-5.15 StartY=7.5972 StartZ=0 EndX=-5.15 EndY=18.9 EndZ=0
    g10: LineSegment StartX=-5.15 StartY=18.9 StartZ=0 EndX=5.15 EndY=18.9 EndZ=0
    g11: LineSegment StartX=5.15 StartY=18.9 StartZ=0 EndX=5.15 EndY=7.5972 EndZ=0
    g12: ArcOfCircle CenterX=0 CenterY=0 CenterZ=0 NormalX=0 NormalY=0 NormalZ=1 AngleXU=0 Radius=9.17824 StartAngle=2.54587 EndAngle=3.73732
    g13: ArcOfCircle CenterX=0 CenterY=0 CenterZ=0 NormalX=0 NormalY=0 NormalZ=1 AngleXU=0 Radius=9.17824 StartAngle=5.68746 EndAngle=6.87891
    g14: ArcOfCircle CenterX=0 CenterY=0 CenterZ=0 NormalX=0 NormalY=0 NormalZ=1 AngleXU=0 Radius=9.17824 StartAngle=4.11666 EndAngle=5.30812
    g15: ArcOfCircle CenterX=0 CenterY=0 CenterZ=0 NormalX=0 NormalY=0 NormalZ=1 AngleXU=0 Radius=9.17824 StartAngle=0.97507 EndAngle=2.16652
  constraints (44):
    c: Coincident(g0,g1)
    c: Coincident(g1,g2)
    c: Vertical(g0)
    c: Vertical(g2)
    c: PointOnObject(g2,g-3)
    c: Coincident(g3,g4)
    c: Coincident(g4,g5)
    c: Horizontal(g3)
    c: Horizontal(g5)
    c: PointOnObject(g3,g-3)
    c: Coincident(g6,g7)
    c: Coincident(g7,g8)
    c: Horizontal(g6)
    c: Horizontal(g8)
    c: PointOnObject(g6,g-3)
    c: Coincident(g9,g10)
    c: Coincident(g10,g11)
    c: Vertical(g9)
    c: Vertical(g11)
    c: PointOnObject(g11,g-3)
    c: Symmetric(g4,g3,g-1)
    c: Symmetric(g7,g6,g-1)
    c: Symmetric(g10,g9,g-2)
    c: Symmetric(g0,g1,g-2)
    c: Equal(g1,g4)
    c: Equal(g4,g10)
    c: Equal(g10,g7)
    c: Equal(g9,g8)
    c: Equal(g8,g0)
    c: Equal(g0,g3)
    c: DistanceY(g4,g4) = 10.3
    c: DistanceX(g4,g-4) = 18.9
    c: Coincident(g12,g-4)
    c: Coincident(g12,g3)
    c: Coincident(g12,g5)
    c: Coincident(g13,g12)
    c: Coincident(g13,g8)
    c: Coincident(g13,g6)
    c: Coincident(g14,g12)
    c: Coincident(g14,g2)
    c: Coincident(g14,g0)
    c: Coincident(g15,g12)
    c: Coincident(g15,g9)
    c: Coincident(g15,g11)
FEATURE [PartDesign::SubShapeBinder] Binder  label="Binder_ContactTop"
  BindCopyOnChange = 0
  BindMode = 0
  ClaimChildren = false
  Context = -> Part001 [Body015.Binder.]
  Fuse = false
  MakeFace = true
  OffsetFill = false
  OffsetIntersection = false
  OffsetJoinType = 0
  OffsetOpenResult = false
  PartialLoad = false
  Relative = true
  Support = -> [Part[Body001.Pocket.Face30,Body001.Pocket.Face26,Body001.Pocket.Face29,Body001.Pocket.Face28]]
  _Version = 2
FEATURE [PartDesign::Pad] Pad001  label="Pad_ContactShell"
  BaseFeature = -> Revolution001
  Direction = (0,-3e-16,-1)
  Length = 10.35
  Length2 = 10
  Placement = pos=(0,0,0) rot=(1,0,0;1.5708rad)
  Profile = -> Sketch004
  ReferenceAxis = -> Sketch004 [N_Axis]
  Type = 0
  expr: Length = <<params>>.sw_to_button_top + <<params>>.arm_height + 1
FEATURE [PartDesign::ShapeBinder] ShapeBinder002  label="ShapeBinder_CShell_bottom"
  Support = -> [Pad001]
  TraceSupport = false
FEATURE [Sketcher::SketchObject] Sketch018  label="Sketch_SW_Housing_cut"
  ExternalGeometry = -> [ShapeBinder002]
  FullyConstrained = true
  MapMode = 5
  Placement = pos=(0,-4.1e-15,-7.35) rot=(1,0,0;3.14159rad)
  Support = -> [Pad001]
  expr: Constraints[10] = <<params>>.ccover_shell_thickness
  expr: Constraints[9] = <<params>>.ccover_shell_thickness
  sketch-geometry (16):
    g0: LineSegment StartX=-8.62076 StartY=3.15 StartZ=0 EndX=-16.9 EndY=3.15 EndZ=0
    g1: LineSegment StartX=-16.9 StartY=3.15 StartZ=0 EndX=-16.9 EndY=-3.15 EndZ=0
    g2: LineSegment StartX=-16.9 StartY=-3.15 StartZ=0 EndX=-8.62076 EndY=-3.15 EndZ=0
    g3: ArcOfCircle CenterX=0 CenterY=0 CenterZ=0 NormalX=0 NormalY=0 NormalZ=1 AngleXU=0 Radius=9.17824 StartAngle=2.79127 EndAngle=3.49192
    g4: LineSegment StartX=-3.15 StartY=8.62076 StartZ=0 EndX=-3.15 EndY=16.9 EndZ=0
    g5: LineSegment StartX=-3.15 StartY=16.9 StartZ=0 EndX=3.15 EndY=16.9 EndZ=0
    g6: LineSegment StartX=3.15 StartY=16.9 StartZ=0 EndX=3.15 EndY=8.62076 EndZ=0
    g7: LineSegment StartX=8.62076 StartY=3.15 StartZ=0 EndX=16.9 EndY=3.15 EndZ=0
    g8: LineSegment StartX=16.9 StartY=3.15 StartZ=0 EndX=16.9 EndY=-3.15 EndZ=0
    g9: LineSegment StartX=16.9 StartY=-3.15 StartZ=0 EndX=8.62076 EndY=-3.15 EndZ=0
    g10: LineSegment StartX=3.15 StartY=-8.62076 StartZ=0 EndX=3.15 EndY=-16.9 EndZ=0
    g11: LineSegment StartX=3.15 StartY=-16.9 StartZ=0 EndX=-3.15 EndY=-16.9 EndZ=0
    g12: LineSegment StartX=-3.15 StartY=-16.9 StartZ=0 EndX=-3.15 EndY=-8.62076 EndZ=0
    g13: ArcOfCircle CenterX=0 CenterY=0 CenterZ=0 NormalX=0 NormalY=0 NormalZ=1 AngleXU=0 Radius=9.17824 StartAngle=4.36206 EndAngle=5.06271
    g14: ArcOfCircle CenterX=0 CenterY=0 CenterZ=0 NormalX=0 NormalY=0 NormalZ=1 AngleXU=0 Radius=9.17824 StartAngle=5.93286 EndAngle=6.63351
    g15: ArcOfCircle CenterX=0 CenterY=0 CenterZ=0 NormalX=0 NormalY=0 NormalZ=1 AngleXU=0 Radius=9.17824 StartAngle=1.22047 EndAngle=1.92112
  constraints (44):
    c: PointOnObject(g0,g-4)
    c: Horizontal(g0)
    c: Coincident(g1,g0)
    c: Coincident(g2,g1)
    c: Horizontal(g2)
    c: Coincident(g3,g-10)
    c: Coincident(g3,g0)
    c: Coincident(g3,g2)
    c: Symmetric(g0,g1,g-1)
    c: DistanceY(g0,g-3) = 2
    c: DistanceX(g-3,g0) = 2
    c: PointOnObject(g4,g-5)
    c: Vertical(g4)
    c: Coincident(g5,g4)
    c: Coincident(g6,g5)
    c: Vertical(g6)
    c: PointOnObject(g7,g-8)
    c: Horizontal(g7)
    c: Coincident(g8,g7)
    c: Coincident(g9,g8)
    c: PointOnObject(g10,g-10)
    c: Vertical(g10)
    c: Coincident(g11,g10)
    c: Vertical(g12)
    c: Equal(g2,g12)
    c: Equal(g12,g9)
    c: Equal(g9,g6)
    c: Coincident(g11,g12)
    c: Equal(g11,g8)
    c: Symmetric(g4,g5,g-2)
    c: Symmetric(g7,g8,g-1)
    c: Symmetric(g10,g11,g-2)
    c: Coincident(g13,g3)
    c: Coincident(g13,g12)
    c: Coincident(g13,g10)
    c: Horizontal(g9)
    c: Equal(g8,g5)
    c: Equal(g11,g1)
    c: Coincident(g14,g3)
    c: Coincident(g14,g9)
    c: Coincident(g14,g7)
    c: Coincident(g15,g3)
    c: Coincident(g15,g6)
    c: Coincident(g15,g4)
FEATURE [PartDesign::Pocket] Pocket003  label="Pocket_SW_housing"
  BaseFeature = -> Pad001
  Direction = (0,4e-16,1)
  Length = 9.35
  Length2 = 5
  Placement = pos=(0,0,0) rot=(1,0,0;1.5708rad)
  Profile = -> Sketch018
  ReferenceAxis = -> Sketch018 [N_Axis]
  Type = 0
  expr: Length = <<params>>.sw_to_button_top + <<params>>.arm_height
FEATURE [PartDesign::ShapeBinder] ShapeBinder015  label="ShapeBinder_CShell_top"
  Support = -> [Pocket003]
  TraceSupport = false
FEATURE [Sketcher::SketchObject] Sketch006  label="Sketch_SW_housing_cap"
  ExternalGeometry = -> [Binder001,ShapeBinder015]
  FullyConstrained = true
  MapMode = 5
  Placement = pos=(0,1.7e-15,3) rot=(0,0,1;3.14159rad)
  Support = -> [Pocket003]
  sketch-geometry (16):
    g0: LineSegment StartX=5.15 StartY=7.5972 StartZ=0 EndX=5.15 EndY=18.9 EndZ=0
    g1: LineSegment StartX=5.15 StartY=18.9 StartZ=0 EndX=-5.15 EndY=18.9 EndZ=0
    g2: LineSegment StartX=-5.15 StartY=18.9 StartZ=0 EndX=-5.15 EndY=7.5972 EndZ=0
    g3: LineSegment StartX=-5.15 StartY=-7.5972 StartZ=0 EndX=-5.15 EndY=-18.9 EndZ=0
    g4: LineSegment StartX=-5.15 StartY=-18.9 StartZ=0 EndX=5.15 EndY=-18.9 EndZ=0
    g5: LineSegment StartX=5.15 StartY=-18.9 StartZ=0 EndX=5.15 EndY=-7.5972 EndZ=0
    g6: LineSegment StartX=18.9 StartY=-5.15 StartZ=0 EndX=7.5972 EndY=-5.15 EndZ=0
    g7: LineSegment StartX=7.5972 StartY=5.15 StartZ=0 EndX=18.9 EndY=5.15 EndZ=0
    g8: LineSegment StartX=18.9 StartY=5.15 StartZ=0 EndX=18.9 EndY=-5.15 EndZ=0
    g9: LineSegment StartX=-18.9 StartY=-5.15 StartZ=0 EndX=-7.5972 EndY=-5.15 EndZ=0
    g10: LineSegment StartX=-7.5972 StartY=5.15 StartZ=0 EndX=-18.9 EndY=5.15 EndZ=0
    g11: LineSegment StartX=-18.9 StartY=5.15 StartZ=0 EndX=-18.9 EndY=-5.15 EndZ=0
    g12: ArcOfCircle CenterX=0 CenterY=3.8e-15 CenterZ=0 NormalX=0 NormalY=0 NormalZ=1 AngleXU=0 Radius=9.17824 StartAngle=2.54587 EndAngle=3.73732
    g13: ArcOfCircle CenterX=0 CenterY=3.8e-15 CenterZ=0 NormalX=0 NormalY=0 NormalZ=1 AngleXU=0 Radius=9.17824 StartAngle=0.97507 EndAngle=2.16652
    g14: ArcOfCircle CenterX=0 CenterY=3.8e-15 CenterZ=0 NormalX=0 NormalY=0 NormalZ=1 AngleXU=0 Radius=9.17824 StartAngle=5.68746 EndAngle=6.87891
    g15: ArcOfCircle CenterX=0 CenterY=3.8e-15 CenterZ=0 NormalX=0 NormalY=0 NormalZ=1 AngleXU=0 Radius=9.17824 StartAngle=4.11666 EndAngle=5.30812
  constraints (40):
    c: Coincident(g0,g1)
    c: Coincident(g1,g2)
    c: Coincident(g3,g4)
    c: Coincident(g4,g5)
    c: Coincident(g7,g8)
    c: Coincident(g8,g6)
    c: Coincident(g10,g11)
    c: Coincident(g11,g9)
    c: Horizontal(g10)
    c: Coincident(g7,g-11)
    c: Horizontal(g7)
    c: Coincident(g1,g-7)
    c: Coincident(g0,g-6)
    c: Vertical(g2)
    c: Vertical(g0)
    c: Horizontal(g6)
    c: Coincident(g4,g-9)
    c: Vertical(g3)
    c: Coincident(g3,g-9)
    c: PointOnObject(g3,g-3)
    c: Vertical(g5)
    c: PointOnObject(g6,g-3)
    c: Coincident(g-11,g6)
    c: Coincident(g-5,g9)
    c: Coincident(g-5,g10)
    c: PointOnObject(g10,g-3)
    c: Horizontal(g9)
    c: Coincident(g12,g-3)
    c: Coincident(g12,g9)
    c: Coincident(g12,g10)
    c: Coincident(g13,g12)
    c: Coincident(g13,g2)
    c: Coincident(g13,g0)
    c: Coincident(g14,g12)
    c: Coincident(g14,g7)
    c: Coincident(g14,g6)
    c: Coincident(g15,g12)
    c: Coincident(g15,g5)
    c: Coincident(g15,g3)
    c: PointOnObject(g0,g-3)
FEATURE [PartDesign::Pad] Pad002  label="Pad_SW_Housing_cap"
  BaseFeature = -> Pocket003
  Direction = (0,6e-16,1)
  Length = 5.5
  Length2 = 10
  Placement = pos=(0,0,0) rot=(1,0,0;1.5708rad)
  Profile = -> Sketch006
  ReferenceAxis = -> Sketch006 [N_Axis]
  Type = 0
FEATURE [PartDesign::Fillet] Fillet007  label="Fillet_InnerCollar"
  Base = -> Pad002
  BaseFeature = -> Pad002
  Placement = pos=(0,0,0) rot=(1,0,0;1.5708rad)
  Radius = 1
  SupportTransform = false
  UseAllEdges = false
FEATURE [PartDesign::ShapeBinder] ShapeBinder014  label="ShapeBinderShellOuter_Base"
  Support = -> [Pad002]
  TraceSupport = false
FEATURE [PartDesign::SubShapeBinder] Binder004  label="Binder_PCB"
  BindCopyOnChange = 0
  BindMode = 0
  ClaimChildren = false
  Context = -> Part001 [Body011.Binder004.]
  Fuse = false
  MakeFace = true
  OffsetFill = false
  OffsetIntersection = false
  OffsetJoinType = 0
  OffsetOpenResult = false
  PartialLoad = false
  Relative = true
  Support = -> [thumbpad_1[Part__Feature166.Face5]]
  _Version = 2
FEATURE [Sketcher::SketchObject] Sketch017  label="Sketch_MountingCollarExtrude"
  ExternalGeometry = -> [ShapeBinder014,Binder004]
  FullyConstrained = false
  MapMode = 5
  Support = -> [XY_Plane036,ShapeBinder014]
  sketch-geometry (11):
    g0: LineSegment StartX=-15.65 StartY=5.15 StartZ=0 EndX=-15.65 EndY=15.65 EndZ=0
    g1: LineSegment StartX=-15.65 StartY=15.65 StartZ=0 EndX=-5.15 EndY=15.65 EndZ=0
    g2: LineSegment StartX=-5.15 StartY=11.15 StartZ=0 EndX=-11.15 EndY=11.15 EndZ=0
    g3: LineSegment StartX=-11.15 StartY=11.15 StartZ=0 EndX=-11.15 EndY=5.15 EndZ=0
    g4: LineSegment StartX=-11.15 StartY=5.15 StartZ=0 EndX=-15.65 EndY=5.15 EndZ=0
    g5: LineSegment StartX=-5.15 StartY=11.15 StartZ=0 EndX=-5.15 EndY=15.65 EndZ=0
    g6: LineSegment StartX=-11.15 StartY=11.15 StartZ=0 EndX=-15.65 EndY=11.15 EndZ=0
    g7: LineSegment StartX=-11.15 StartY=11.15 StartZ=0 EndX=-11.15 EndY=15.65 EndZ=0
    g8: Circle CenterX=-13 CenterY=13 CenterZ=0 NormalX=0 NormalY=0 NormalZ=1 AngleXU=0 Radius=1.6
    g9: LineSegment StartX=-13 StartY=13 StartZ=0 EndX=-13 EndY=15.65 EndZ=0
    g10: LineSegment StartX=-13 StartY=13 StartZ=0 EndX=-15.65 EndY=13 EndZ=0
  constraints (26):
    c: Vertical(g0)
    c: Coincident(g1,g0)
    c: Horizontal(g1)
    c: Horizontal(g2)
    c: Coincident(g3,g2)
    c: Vertical(g3)
    c: Coincident(g4,g3)
    c: Coincident(g4,g0)
    c: Coincident(g5,g2)
    c: Coincident(g5,g1)
    c: Coincident(g6,g2)
    c: PointOnObject(g6,g0)
    c: Horizontal(g6)
    c: Coincident(g7,g2)
    c: PointOnObject(g7,g1)
    c: Vertical(g7)
    c: Equal(g6,g7)
    c: Equal(g3,g2)
    c: Coincident(g9,g8)
    c: PointOnObject(g9,g1)
    c: Vertical(g9)
    c: Coincident(g10,g8)
    c: PointOnObject(g10,g0)
    c: Horizontal(g10)
    c: DistanceY(g5,g5) = 4.5
    c: DistanceX(g2,g2) = 6
FEATURE [PartDesign::Pad] Pad008  label="Pad_MountingColarExtrude"
  Direction = (0,0,1)
  Length = 2
  Length2 = 10
  Profile = -> Sketch017
  ReferenceAxis = -> Sketch017 [N_Axis]
  Type = 0
FEATURE [PartDesign::Fillet] Fillet006
  Base = -> Pad008 [Edge11,Edge2]
  BaseFeature = -> Pad008
  Radius = 1
  SupportTransform = false
  UseAllEdges = false
FEATURE [PartDesign::Body] Body011  label="MountingHoleCollar"
  Group = -> [ShapeBinder014,Binder004,Sketch017,Pad008,Fillet006]
  Origin = -> Origin036
  Placement = pos=(0,0,-7.35) rot=(0,0,1;0rad)
  Tip = -> Fillet006
FEATURE [PartDesign::ShapeBinder] ShapeBinder016  label="ShapeBinder_AlignmentCutout"
  Support = -> [Pad002]
  TraceSupport = false
FEATURE [PartDesign::ShapeBinder] ShapeBinder017  label="ShapeBinder_ContactArm"
  Support = -> [Fillet005]
  TraceSupport = false
FEATURE [Sketcher::SketchObject] Sketch019  label="Sketch_ArmPockets"
  ExternalGeometry = -> [ShapeBinder016,ShapeBinder017]
  FullyConstrained = true
  MapMode = 5
  Placement = pos=(0,1.3e-15,2) rot=(1,0,0;3.14159rad)
  Support = -> [Pad002]
  sketch-geometry (43):
    g0: ArcOfCircle CenterX=0 CenterY=0 CenterZ=0 NormalX=0 NormalY=0 NormalZ=1 AngleXU=0 Radius=9.17824 StartAngle=3.30024 EndAngle=3.49192
    g1: ArcOfCircle CenterX=0 CenterY=0 CenterZ=0 NormalX=0 NormalY=0 NormalZ=1 AngleXU=0 Radius=9.17824 StartAngle=2.79127 EndAngle=2.98295
    g2: LineSegment StartX=-16.9 StartY=3.15 StartZ=0 EndX=-8.62076 EndY=3.15 EndZ=0
    g3: LineSegment StartX=-16.9 StartY=3.15 StartZ=0 EndX=-16.9 EndY=-3.15 EndZ=0
    g4: LineSegment StartX=-16.9 StartY=-3.15 StartZ=0 EndX=-8.62076 EndY=-3.15 EndZ=0
    g5: LineSegment StartX=-9.06297 StartY=-1.45 StartZ=0 EndX=-13.9 EndY=-1.45 EndZ=0
    g6: LineSegment StartX=-13.9 StartY=1.45 StartZ=0 EndX=-9.06297 EndY=1.45 EndZ=0
    g7: LineSegment StartX=-3.15 StartY=8.62076 StartZ=0 EndX=-3.15 EndY=16.9 EndZ=0
    g8: LineSegment StartX=-3.15 StartY=16.9 StartZ=0 EndX=3.15 EndY=16.9 EndZ=0
    g9: LineSegment StartX=3.15 StartY=16.9 StartZ=0 EndX=3.15 EndY=8.62076 EndZ=0
    g10: LineSegment StartX=8.62076 StartY=3.15 StartZ=0 EndX=16.9 EndY=3.15 EndZ=0
    g11: LineSegment StartX=16.9 StartY=3.15 StartZ=0 EndX=16.9 EndY=-3.15 EndZ=0
    g12: LineSegment StartX=16.9 StartY=-3.15 StartZ=0 EndX=8.62076 EndY=-3.15 EndZ=0
    g13: LineSegment StartX=3.15 StartY=-16.9 StartZ=0 EndX=-3.15 EndY=-16.9 EndZ=0
    g14: LineSegment StartX=-3.15 StartY=-16.9 StartZ=0 EndX=-3.15 EndY=-8.62076 EndZ=0
    g15: LineSegment StartX=3.15 StartY=-8.62076 StartZ=0 EndX=3.15 EndY=-16.9 EndZ=0
    g16: ArcOfCircle CenterX=0 CenterY=0 CenterZ=0 NormalX=0 NormalY=0 NormalZ=1 AngleXU=0 Radius=9.17824 StartAngle=4.87104 EndAngle=5.06271
    g17: ArcOfCircle CenterX=0 CenterY=0 CenterZ=0 NormalX=0 NormalY=0 NormalZ=1 AngleXU=0 Radius=9.17824 StartAngle=4.36206 EndAngle=4.55374
    g18: ArcOfCircle CenterX=0 CenterY=0 CenterZ=0 NormalX=0 NormalY=0 NormalZ=1 AngleXU=0 Radius=9.17824 StartAngle=0.158647 EndAngle=0.350325
    g19: ArcOfCircle CenterX=0 CenterY=0 CenterZ=0 NormalX=0 NormalY=0 NormalZ=1 AngleXU=0 Radius=9.17824 StartAngle=5.93286 EndAngle=6.12454
    g20: ArcOfCircle CenterX=0 CenterY=0 CenterZ=0 NormalX=0 NormalY=0 NormalZ=1 AngleXU=0 Radius=9.17824 StartAngle=1.72944 EndAngle=1.92112
    g21: ArcOfCircle CenterX=0 CenterY=0 CenterZ=0 NormalX=0 NormalY=0 NormalZ=1 AngleXU=0 Radius=9.17824 StartAngle=1.22047 EndAngle=1.41215
    g22: LineSegment StartX=-1.45 StartY=9.06297 StartZ=0 EndX=-1.45 EndY=13.9 EndZ=0
    g23: LineSegment StartX=-1.45 StartY=13.9 StartZ=0 EndX=1.45 EndY=13.9 EndZ=0
    g24: LineSegment StartX=1.45 StartY=13.9 StartZ=0 EndX=1.45 EndY=9.06297 EndZ=0
    g25: LineSegment StartX=1.45 StartY=-9.06297 StartZ=0 EndX=1.45 EndY=-13.9 EndZ=0
    g26: LineSegment StartX=1.45 StartY=-13.9 StartZ=0 EndX=-1.45 EndY=-13.9 EndZ=0
    g27: LineSegment StartX=-1.45 StartY=-13.9 StartZ=0 EndX=-1.45 EndY=-9.06297 EndZ=0
    g28: LineSegment StartX=9.06297 StartY=-1.45 StartZ=0 EndX=13.9 EndY=-1.45 EndZ=0
    g29: LineSegment StartX=13.9 StartY=-1.45 StartZ=0 EndX=13.9 EndY=1.45 EndZ=0
    g30: LineSegment StartX=13.9 StartY=1.45 StartZ=0 EndX=9.06297 EndY=1.45 EndZ=0
    g31: LineSegment StartX=-13.9 StartY=1.45 StartZ=0 EndX=-14.4 EndY=1.45 EndZ=0
    g32: LineSegment StartX=-14.4 StartY=1.45 StartZ=0 EndX=-14.4 EndY=-1.45 EndZ=0
    g33: LineSegment StartX=-14.4 StartY=-1.45 StartZ=0 EndX=-13.9 EndY=-1.45 EndZ=0
    g34: LineSegment StartX=-1.45 StartY=-13.9 StartZ=0 EndX=-1.45 EndY=-14.4 EndZ=0
    g35: LineSegment StartX=-1.45 StartY=-14.4 StartZ=0 EndX=1.45 EndY=-14.4 EndZ=0
    g36: LineSegment StartX=1.45 StartY=-14.4 StartZ=0 EndX=1.45 EndY=-13.9 EndZ=0
    g37: LineSegment StartX=13.9 StartY=-1.45 StartZ=0 EndX=14.4 EndY=-1.45 EndZ=0
    g38: LineSegment StartX=14.4 StartY=-1.45 StartZ=0 EndX=14.4 EndY=1.45 EndZ=0
    g39: LineSegment StartX=14.4 StartY=1.45 StartZ=0 EndX=13.9 EndY=1.45 EndZ=0
    g40: LineSegment StartX=-1.45 StartY=13.9 StartZ=0 EndX=-1.45 EndY=14.4 EndZ=0
    g41: LineSegment StartX=-1.45 StartY=14.4 StartZ=0 EndX=1.45 EndY=14.4 EndZ=0
    g42: LineSegment StartX=1.45 StartY=14.4 StartZ=0 EndX=1.45 EndY=13.9 EndZ=0
  constraints (105):
    c: Coincident(g0,g-6)
    c: Coincident(g0,g-6)
    c: PointOnObject(g0,g-7)
    c: Coincident(g1,g0)
    c: Coincident(g1,g-6)
    c: PointOnObject(g1,g-9)
    c: Coincident(g2,g-4)
    c: Coincident(g2,g1)
    c: Coincident(g3,g2)
    c: Coincident(g3,g-5)
    c: Coincident(g4,g3)
    c: Coincident(g4,g0)
    c: Coincident(g5,g0)
    c: Coincident(g5,g-8)
    c: Coincident(g6,g1)
    c: Coincident(g7,g-19)
    c: Coincident(g7,g-19)
    c: Coincident(g8,g7)
    c: Coincident(g8,g-18)
    c: Coincident(g9,g8)
    c: Coincident(g9,g-18)
    c: Coincident(g10,g-16)
    c: Coincident(g10,g-16)
    c: Coincident(g11,g10)
    c: Coincident(g11,g-15)
    c: Coincident(g12,g11)
    c: Coincident(g12,g-15)
    c: Coincident(g13,g-13)
    c: Coincident(g13,g-13)
    c: Coincident(g14,g13)
    c: Coincident(g14,g-11)
    c: Coincident(g15,g-12)
    c: Coincident(g15,g13)
    c: Coincident(g16,g0)
    c: Coincident(g16,g15)
    c: Coincident(g17,g0)
    c: Coincident(g17,g14)
    c: Coincident(g18,g0)
    c: Coincident(g18,g10)
    c: Coincident(g19,g0)
    c: Coincident(g20,g0)
    c: Coincident(g20,g7)
    c: Coincident(g21,g0)
    c: Coincident(g21,g9)
    c: Coincident(g22,g20)
    c: Vertical(g22)
    c: Coincident(g23,g22)
    c: Coincident(g24,g23)
    c: Coincident(g24,g21)
    c: Vertical(g24)
    c: Coincident(g25,g16)
    c: Vertical(g25)
    c: Coincident(g26,g25)
    c: Coincident(g27,g26)
    c: Coincident(g27,g17)
    c: Vertical(g27)
    c: Coincident(g28,g19)
    c: Horizontal(g28)
    c: Coincident(g29,g28)
    c: Coincident(g30,g29)
    c: Coincident(g30,g18)
    c: Horizontal(g30)
    c: Equal(g5,g27)
    c: Equal(g27,g28)
    c: Equal(g28,g24)
    c: Equal(g29,g26)
    c: Equal(g26,g23)
    c: Symmetric(g22,g23,g-2)
    c: Symmetric(g29,g28,g-1)
    c: Symmetric(g25,g26,g-2)
    c: Coincident(g31,g6)
    c: Horizontal(g31)
    c: Coincident(g32,g31)
    c: Vertical(g32)
    c: Coincident(g33,g32)
    c: Coincident(g33,g5)
    c: Horizontal(g33)
    c: Coincident(g6,g-9)
    c: DistanceX(g31,g31) = 0.5
    c: Coincident(g34,g26)
    c: Vertical(g34)
    c: Coincident(g35,g34)
    c: Horizontal(g35)
    c: Coincident(g36,g35)
    c: Coincident(g36,g25)
    c: Vertical(g36)
    c: Coincident(g37,g28)
    c: Horizontal(g37)
    c: Coincident(g38,g37)
    c: Vertical(g38)
    c: Coincident(g39,g38)
    c: Coincident(g39,g30)
    c: Coincident(g40,g22)
    c: Vertical(g40)
    c: Coincident(g41,g40)
    c: Horizontal(g41)
    c: Coincident(g42,g41)
    c: Coincident(g42,g23)
    c: Vertical(g42)
    c: Equal(g42,g39)
    c: Equal(g39,g36)
    c: Equal(g36,g33)
    c: Equal(g35,g38)
    c: Equal(g41,g32)
    c: Coincident(g19,g12)
FEATURE [PartDesign::Pad] Pad009  label="Pad_ArmPockets"
  BaseFeature = -> Fillet007
  Direction = (0,-7e-16,-1)
  Length = 2.9
  Length2 = 10
  Placement = pos=(0,0,0) rot=(1,0,0;1.5708rad)
  Profile = -> Sketch019
  ReferenceAxis = -> Sketch019 [N_Axis]
  Type = 0
  expr: Length = <<params>>.sw_button_width
FEATURE [PartDesign::Fillet] Fillet  label="Fillet_PocketWiggleRoom"
  Base = -> Pad009 [Edge192,Edge172,Edge152,Edge132]
  BaseFeature = -> Pad009
  Placement = pos=(0,0,0) rot=(1,0,0;1.5708rad)
  Radius = 1
  SupportTransform = false
  UseAllEdges = false
FEATURE [PartDesign::Fillet] Fillet008  label="Fillet_Collar"
  Base = -> Fillet [Edge128]
  BaseFeature = -> Fillet
  Placement = pos=(0,0,0) rot=(1,0,0;1.5708rad)
  Radius = 1
  SupportTransform = false
  UseAllEdges = false
FEATURE [PartDesign::Fillet] Fillet009  label="Fillet_Ends"
  Base = -> Fillet008 [Edge111,Edge108,Edge115,Edge117]
  BaseFeature = -> Fillet008
  Placement = pos=(0,0,0) rot=(1,0,0;1.5708rad)
  Radius = 1
  SupportTransform = false
  UseAllEdges = false
FEATURE [PartDesign::Fillet] Fillet010  label="Fillet_CenterSmoothing"
  Base = -> Fillet009 [Edge9,Edge28,Edge20,Edge48,Edge43,Edge42,Edge36,Edge35]
  BaseFeature = -> Fillet009
  Placement = pos=(0,0,0) rot=(1,0,0;1.5708rad)
  Radius = 2
  SupportTransform = false
  UseAllEdges = false
FEATURE [PartDesign::ShapeBinder] ShapeBinder009  label="ShapeBinder_Pinplacement_2"
  Placement = pos=(0,0,0) rot=(1,0,0;1.5708rad)
  Support = -> [Fillet010]
  TraceSupport = false
FEATURE [Sketcher::SketchObject] Sketch014  label="Sketch_AlignmentPin_2"
  ExternalGeometry = -> [ShapeBinder009]
  FullyConstrained = false
  MapMode = 5
  Placement = pos=(0,-4.1e-15,-7.35) rot=(1,0,0;3.14159rad)
  Support = -> [ShapeBinder009]
  sketch-geometry (4):
    g0: Circle CenterX=-9.18642 CenterY=-4.15 CenterZ=0 NormalX=0 NormalY=0 NormalZ=1 AngleXU=0 Radius=0.8
    g1: LineSegment StartX=-9.18642 StartY=-4.15 StartZ=0 EndX=-9.18642 EndY=-3.15 EndZ=0
    g2: LineSegment StartX=-9.18642 StartY=-4.15 StartZ=0 EndX=-9.18642 EndY=-5.15 EndZ=0
    g3: LineSegment StartX=-9.18642 StartY=-4.15 StartZ=0 EndX=-8.18642 EndY=-4.15 EndZ=0
  constraints (9):
    c: Diameter(g0) = 1.6
    c: Coincident(g0,g1)
    c: Coincident(g2,g0)
    c: Vertical(g1)
    c: Coincident(g3,g0)
    c: Equal(g2,g1)
    c: Vertical(g2)
    c: Horizontal(g3)
    c: Equal(g3,g2)
FEATURE [PartDesign::Pad] Pad007  label="Pad_AlignmentPin_2"
  Direction = (0,-8e-16,-1)
  Length = 1.92
  Length2 = 10
  Placement = pos=(0,0,0) rot=(1,0,0;1.5708rad)
  Profile = -> Sketch014
  ReferenceAxis = -> Sketch014 [N_Axis]
  Type = 0
  expr: Length = <<params>>.pcb_thickness * 1.2
FEATURE [PartDesign::Body] Body009  label="BoardPin2"
  Group = -> [ShapeBinder009,Sketch014,Pad007]
  Origin = -> Origin023
  Tip = -> Pad007
FEATURE [PartDesign::ShapeBinder] ShapeBinder008  label="ShapeBinder_Pinplacement_1"
  Placement = pos=(0,0,0) rot=(1,0,0;1.5708rad)
  Support = -> [Fillet010]
  TraceSupport = false
FEATURE [Sketcher::SketchObject] Sketch013  label="Sketch_AlignmentPin_1"
  ExternalGeometry = -> [ShapeBinder008]
  FullyConstrained = false
  MapMode = 5
  Placement = pos=(0,-4.1e-15,-7.35) rot=(1,0,0;3.14159rad)
  Support = -> [ShapeBinder008]
  sketch-geometry (4):
    g0: Circle CenterX=-9.18642 CenterY=4.15 CenterZ=0 NormalX=0 NormalY=0 NormalZ=1 AngleXU=0 Radius=0.8
    g1: LineSegment StartX=-9.18642 StartY=4.15 StartZ=0 EndX=-8.18642 EndY=4.15 EndZ=0
    g2: LineSegment StartX=-9.18642 StartY=4.15 StartZ=0 EndX=-9.18642 EndY=5.15 EndZ=0
    g3: LineSegment StartX=-9.18642 StartY=4.15 StartZ=0 EndX=-9.18642 EndY=3.15 EndZ=0
  constraints (9):
    c: Coincident(g1,g0)
    c: Horizontal(g1)
    c: Coincident(g2,g0)
    c: Vertical(g2)
    c: Coincident(g3,g0)
    c: Vertical(g3)
    c: Equal(g2,g1)
    c: Equal(g1,g3)
    c: Diameter(g0) = 1.6
FEATURE [PartDesign::Pad] Pad006  label="Pad_AlignmentPin_1"
  Direction = (0,-8e-16,-1)
  Length = 1.92
  Length2 = 10
  Placement = pos=(0,0,0) rot=(1,0,0;1.5708rad)
  Profile = -> Sketch013
  ReferenceAxis = -> Sketch013 [N_Axis]
  Type = 0
  expr: Length = <<params>>.pcb_thickness * 1.2
FEATURE [PartDesign::Body] Body008  label="BoardPin1"
  Group = -> [ShapeBinder008,Sketch013,Pad006]
  Origin = -> Origin022
  Tip = -> Pad006
FEATURE [PartDesign::Body] Body002  label="OuterShell"
  Group = -> [Sketch003,Revolution001,Binder001,ShapeBinder001,Sketch004,Binder,Pad001,Pocket003,Sketch006,Pad002,ShapeBinder002,Sketch018,ShapeBinder015,Fillet007,ShapeBinder016,ShapeBinder017,Sketch019,Pad009,Fillet,Fillet008,Fillet009,Fillet010]
  Origin = -> Origin004
  Tip = -> Fillet010
FEATURE [PartDesign::FeatureBase] Clone001
  BaseFeature = -> Body002
FEATURE [PartDesign::Body] Body013  label="CenterBody"
  Group = -> [Clone001]
  Origin = -> Origin039
  Tip = -> Clone001
FEATURE [PartDesign::FeatureBase] Clone002
  BaseFeature = -> Body011
  Placement = pos=(0,0,-7.35) rot=(0,0,1;0rad)
FEATURE [PartDesign::Body] Body014  label="Collar1"
  Group = -> [Clone002]
  Origin = -> Origin040
  Tip = -> Clone002
FEATURE [PartDesign::FeatureBase] Clone004
  BaseFeature = -> Body009
FEATURE [PartDesign::Body] Body016  label="Pin1"
  Group = -> [Clone004]
  Origin = -> Origin042
  Tip = -> Clone004
FEATURE [PartDesign::FeatureBase] Clone005
  BaseFeature = -> Body008
FEATURE [PartDesign::Body] Body017  label="Pin2"
  Group = -> [Clone005]
  Origin = -> Origin043
  Tip = -> Clone005
FEATURE [Part::Feature] trajectory_line
  shape: bbox 2e-07 x 2e-07 x 38 mm, 0 faces, 0 solids (baked)
FEATURE [App::DocumentObjectGroupPython] SimpleGroup  label="EA_Stick"  # scripted group (container) (typed FeaturePython)
  AnimationStepTime = 0
  AnimationSteps = 20
  Distance = 38
  Group = -> [trajectory_line]
  Revolutions = 0
  dir_vectors = (1) [(0,0,1)]
  rot_centers = (1) [(-1.74868e-11,-1.04491e-11,3.5)]
  rot_vectors = (1) [(0,0,-1)]
FEATURE [Part::Feature] trajectory_line001
  shape: bbox 2e-07 x 2e-07 x 10 mm, 0 faces, 0 solids (baked)
FEATURE [App::DocumentObjectGroupPython] SimpleGroup008  label="EA_Nut_ConnSide"  # scripted group (container) (typed FeaturePython)
  AnimationStepTime = 0
  AnimationSteps = 20
  Distance = 10
  Group = -> [trajectory_line001]
  Revolutions = 0
  dir_vectors = (1) [(0,0,-1)]
  rot_centers = (1) [(-12.9,13,-11.8)]
  rot_vectors = (1) [(0,0,-1)]
FEATURE [Part::Feature] trajectory_line002
  shape: bbox 2e-07 x 2e-07 x 8 mm, 0 faces, 0 solids (baked)
FEATURE [App::DocumentObjectGroupPython] SimpleGroup009  label="EA_Washer_ConnSide"  # scripted group (container) (typed FeaturePython)
  AnimationStepTime = 0
  AnimationSteps = 20
  Distance = 8
  Group = -> [trajectory_line002]
  Revolutions = 0
  dir_vectors = (1) [(0,0,-1)]
  rot_centers = (1) [(-13,13,-9.5)]
  rot_vectors = (1) [(0,0,-1)]
FEATURE [Part::Feature] trajectory_line003
  shape: bbox 2e-07 x 2e-07 x 10 mm, 0 faces, 0 solids (baked)
FEATURE [App::DocumentObjectGroupPython] SimpleGroup012  label="EA_Nut_Back"  # scripted group (container) (typed FeaturePython)
  AnimationStepTime = 0
  AnimationSteps = 20
  Distance = 10
  Group = -> [trajectory_line003]
  Revolutions = 0
  dir_vectors = (1) [(0,0,-1)]
  rot_centers = (1) [(12.9,-13,-11.8)]
  rot_vectors = (1) [(0,0,-1)]
FEATURE [Part::Feature] trajectory_line004
  shape: bbox 2e-07 x 2e-07 x 8 mm, 0 faces, 0 solids (baked)
FEATURE [App::DocumentObjectGroupPython] SimpleGroup013  label="EA_Wash_Back"  # scripted group (container) (typed FeaturePython)
  AnimationStepTime = 0
  AnimationSteps = 20
  Distance = 8
  Group = -> [trajectory_line004]
  Revolutions = 0
  dir_vectors = (1) [(0,0,-1)]
  rot_centers = (1) [(13,-13,-9.5)]
  rot_vectors = (1) [(0,0,-1)]
FEATURE [Part::Feature] trajectory_line005
  shape: bbox 2e-07 x 2e-07 x 38 mm, 0 faces, 0 solids (baked)
FEATURE [App::DocumentObjectGroupPython] SimpleGroup007  label="EA_Screw_ConnSide"  # scripted group (container) (typed FeaturePython)
  AnimationStepTime = 0
  AnimationSteps = 20
  Distance = 38
  Group = -> [trajectory_line005]
  Revolutions = 0
  dir_vectors = (1) [(0,0,1)]
  rot_centers = (1) [(-13,13,-4.42354)]
  rot_vectors = (1) [(0.5,0,0.866025)]
FEATURE [Part::Feature] trajectory_line006
  shape: bbox 2e-07 x 2e-07 x 38 mm, 0 faces, 0 solids (baked)
FEATURE [App::DocumentObjectGroupPython] SimpleGroup011  label="EA_Screw_Back"  # scripted group (container) (typed FeaturePython)
  AnimationStepTime = 0
  AnimationSteps = 20
  Distance = 38
  Group = -> [trajectory_line006]
  Revolutions = 0
  dir_vectors = (1) [(0,0,1)]
  rot_centers = (1) [(13,-13,-4.78629)]
  rot_vectors = (1) [(0,0,1)]
FEATURE [Part::Feature] trajectory_line012
  shape: bbox 2e-07 x 2e-07 x 5 mm, 0 faces, 0 solids (baked)
FEATURE [App::DocumentObjectGroupPython] SimpleGroup001  label="EA_ShellInner"  # scripted group (container) (typed FeaturePython)
  AnimationStepTime = 0
  AnimationSteps = 20
  Distance = 5
  Group = -> [trajectory_line012]
  Revolutions = 0
  dir_vectors = (1) [(0,0,1)]
  rot_centers = (1) [(2.28183e-11,1.3633e-11,10.5)]
  rot_vectors = (1) [(0,0,1)]
FEATURE [Part::Feature] trajectory_line013
  shape: bbox 2e-07 x 2e-07 x 20 mm, 0 faces, 0 solids (baked)
FEATURE [App::DocumentObjectGroupPython] SimpleGroup015  label="EA_ShellOuter"  # scripted group (container) (typed FeaturePython)
  AnimationStepTime = 0
  AnimationSteps = 20
  Distance = 25
  Group = -> [trajectory_line013]
  Revolutions = 0
  dir_vectors = (1) [(0,7.8e-16,1)]
  rot_centers = (1) [(2.07392e-10,-13.2472,8.5)]
  rot_vectors = (1) [(0,7.8e-16,1)]
FEATURE [App::DocumentObjectGroupPython] ExplodedAssembly  # scripted group (container) (typed FeaturePython)
  AnimationStep = 0
  CurrentTrajectory = 0
  Group = -> [SimpleGroup,SimpleGroup008,SimpleGroup009,SimpleGroup012,SimpleGroup013,SimpleGroup007,SimpleGroup011,SimpleGroup015,SimpleGroup001]
  InAnimation = false
  RemoveAllTrajectories = false
  ResetAnimation = false
FEATURE [PartDesign::FeatureBase] Clone006
  BaseFeature = -> Body011
  Placement = pos=(0,0,-7.35) rot=(0,0,1;0rad)
FEATURE [PartDesign::Body] Body018  label="MountingHoleCollar_2"
  Group = -> [Clone006]
  Origin = -> Origin044
  Placement = pos=(0,0,0) rot=(0,0,1;3.14159rad)
  Tip = -> Clone006
FEATURE [App::Part] Part001  label="SwivelHousing"
  Group = -> [Body008,Body009,Body002,Body011,Body018]
  Origin = -> Origin003
FEATURE [PartDesign::FeatureBase] Clone
  BaseFeature = -> Body018
  Placement = pos=(0,0,0) rot=(0,0,1;3.14159rad)
FEATURE [PartDesign::Body] Body019  label="Collar2"
  Group = -> [Clone]
  Origin = -> Origin045
  Tip = -> Clone
FEATURE [App::Part] Part004  label="FusionClone"
  Group = -> [Body013,Body014,Body016,Body017,Body019]
  Origin = -> Origin038
FEATURE [PartDesign::FeatureBase] Clone008
  BaseFeature = -> Body008
FEATURE [PartDesign::Body] Body021  label="BP1"
  Group = -> [Clone008]
  Origin = -> Origin048
  Tip = -> Clone008
FEATURE [PartDesign::FeatureBase] Clone009
  BaseFeature = -> Body009
FEATURE [PartDesign::Body] Body022  label="BP2"
  Group = -> [Clone009]
  Origin = -> Origin049
  Tip = -> Clone009
FEATURE [PartDesign::FeatureBase] Clone010
  BaseFeature = -> Body002
FEATURE [PartDesign::FeatureBase] Clone011
  BaseFeature = -> Body011
  Placement = pos=(0,0,-7.35) rot=(0,0,1;0rad)
FEATURE [PartDesign::Body] Body024  label="Collar003"
  Group = -> [Clone011]
  Origin = -> Origin051
  Tip = -> Clone011
FEATURE [PartDesign::FeatureBase] Clone012
  BaseFeature = -> Body018
  Placement = pos=(0,0,0) rot=(0,0,1;3.14159rad)
FEATURE [PartDesign::Body] Body025  label="Collar004"
  Group = -> [Clone012]
  Origin = -> Origin052
  Tip = -> Clone012
FEATURE [PartDesign::FeatureBase] Clone013
  BaseFeature = -> Body001
FEATURE [PartDesign::Body] Body026  label="CenterShell"
  Group = -> [Clone013]
  Origin = -> Origin053
  Tip = -> Clone013
FEATURE [PartDesign::FeatureBase] Clone014
  BaseFeature = -> Body010
FEATURE [PartDesign::Body] Body027  label="PCB_3DPrintEdit"
  Group = -> [Clone014]
  Origin = -> Origin054
  Placement = pos=(0,0,-8.95) rot=(0,0,1;0rad)
  Tip = -> Clone014
FEATURE [PartDesign::Boolean] Boolean001
  BaseFeature = -> Clone010
  Group = -> [Body021,Body022,Body024,Body025]
  Type = 0
FEATURE [PartDesign::Body] Body023  label="OuterShell001"
  Group = -> [Clone010,Boolean001]
  Origin = -> Origin050
  Tip = -> Boolean001
FEATURE [PartDesign::ShapeBinder] ShapeBinder018  label="ShapeBinder_PCBSurface"
  Support = -> [Part__Feature166]
  TraceSupport = false
FEATURE [Sketcher::SketchObject] Sketch020  label="Sketch_Top"
  ExternalGeometry = -> [ShapeBinder018]
  FullyConstrained = true
  MapMode = 5
  Support = -> [XY_Plane056]
  expr: Constraints[37] = (<<params>>.insert_hole_dia + <<params>>.insert_min_wall_thickness) / 2
  sketch-geometry (14):
    g0: LineSegment StartX=15.8 StartY=-15.8 StartZ=0 EndX=15.8 EndY=15.8 EndZ=0
    g1: LineSegment StartX=15.8 StartY=15.8 StartZ=0 EndX=-15.8 EndY=15.8 EndZ=0
    g2: LineSegment StartX=-15.8 StartY=15.8 StartZ=0 EndX=-15.8 EndY=-15.8 EndZ=0
    g3: LineSegment StartX=-15.8 StartY=-15.8 StartZ=0 EndX=15.8 EndY=-15.8 EndZ=0
    g4: GeomPoint X=0 Y=0 Z=0
    g5: LineSegment StartX=0 StartY=8 StartZ=0 EndX=-5.65685 EndY=5.65685 EndZ=0
    g6: LineSegment StartX=-5.65685 StartY=5.65685 StartZ=0 EndX=-8 EndY=9e-16 EndZ=0
    g7: LineSegment StartX=-8 StartY=9e-16 StartZ=0 EndX=-5.65685 EndY=-5.65685 EndZ=0
    g8: LineSegment StartX=-5.65685 StartY=-5.65685 StartZ=0 EndX=0 EndY=-8 EndZ=0
    g9: LineSegment StartX=-3e-16 StartY=-8 StartZ=0 EndX=5.65685 EndY=-5.65685 EndZ=0
    g10: LineSegment StartX=5.65685 StartY=-5.65685 StartZ=0 EndX=8 EndY=-9e-16 EndZ=0
    g11: LineSegment StartX=8 StartY=-1e-15 StartZ=0 EndX=5.65685 EndY=5.65685 EndZ=0
    g12: LineSegment StartX=5.65685 StartY=5.65685 StartZ=0 EndX=0 EndY=8 EndZ=0
    g13: Circle CenterX=0 CenterY=0 CenterZ=0 NormalX=0 NormalY=0 NormalZ=1 AngleXU=0 Radius=8
  constraints (34):
    c: Coincident(g0,g1)
    c: Coincident(g1,g2)
    c: Coincident(g2,g3)
    c: Coincident(g3,g0)
    c: Horizontal(g1)
    c: Horizontal(g3)
    c: Vertical(g0)
    c: Vertical(g2)
    c: Symmetric(g1,g0,g4)
    c: Coincident(g4,g-1)
    c: Coincident(g5,g6)
    c: Coincident(g6,g7)
    c: Coincident(g7,g8)
    c: Coincident(g8,g9)
    c: Coincident(g9,g10)
    c: Coincident(g10,g11)
    c: Coincident(g11,g12)
    c: Coincident(g12,g5)
    c: Equal(g5, g6-g12) x7
    c: PointOnObject(g5,g13)
    c: PointOnObject(g6,g13)
    c: PointOnObject(g7,g13)
    c: PointOnObject(g8,g13)
    c: PointOnObject(g9,g13)
    c: PointOnObject(g10,g13)
    c: PointOnObject(g11,g13)
    c: PointOnObject(g12,g13)
    c: Coincident(g13,g4)
    c: Equal(g2,g3)
    c: PointOnObject(g5,g-2)
    c: DistanceY(g4,g5) = 8
    c: DistanceX(g1,g-3) = 2.8
    c: DistanceX(g3,g3) = 31.6
    c: DistanceY(g0,g0) = 31.6
FEATURE [PartDesign::Pad] Pad010  label="Pad_SocketTop"
  Direction = (0,0,1)
  Length = 4
  Length2 = 10
  Profile = -> Sketch020
  ReferenceAxis = -> Sketch020 [N_Axis]
  Reversed = true
  Type = 0
FEATURE [PartDesign::Chamfer] Chamfer
  Angle = 45
  Base = -> Pad010 [Edge35,Edge33,Edge30,Edge27,Edge24,Edge21,Edge18,Edge15]
  BaseFeature = -> Pad010
  ChamferType = 0
  FlipDirection = false
  Size = 3
  Size2 = 1
  SupportTransform = false
  UseAllEdges = false
FEATURE [PartDesign::Fillet] Fillet011
  Base = -> Chamfer [Edge10,Edge8,Edge25,Edge49,Edge52,Edge37,Edge51,Edge50]
  BaseFeature = -> Chamfer
  Radius = 2
  SupportTransform = false
  UseAllEdges = false
FEATURE [Sketcher::SketchObject] Sketch021  label="Sketch_InsertBase"
  ExternalGeometry = -> [Fillet011]
  FullyConstrained = true
  MapMode = 5
  Placement = pos=(0,0,-4) rot=(1,0,0;3.14159rad)
  Support = -> [Fillet011]
  expr: Constraints[43] = <<params>>.insert_hole_dia + <<params>>.insert_min_wall_thickness
  sketch-geometry (16):
    g0: LineSegment StartX=-15.8 StartY=-15.8 StartZ=0 EndX=-10.2 EndY=-15.8 EndZ=0
    g1: LineSegment StartX=-10.2 StartY=-15.8 StartZ=0 EndX=-10.2 EndY=-10.2 EndZ=0
    g2: LineSegment StartX=-10.2 StartY=-10.2 StartZ=0 EndX=-15.8 EndY=-10.2 EndZ=0
    g3: LineSegment StartX=-15.8 StartY=-10.2 StartZ=0 EndX=-15.8 EndY=-15.8 EndZ=0
    g4: LineSegment StartX=15.8 StartY=-15.8 StartZ=0 EndX=10.2 EndY=-15.8 EndZ=0
    g5: LineSegment StartX=10.2 StartY=-15.8 StartZ=0 EndX=10.2 EndY=-10.2 EndZ=0
    g6: LineSegment StartX=10.2 StartY=-10.2 StartZ=0 EndX=15.8 EndY=-10.2 EndZ=0
    g7: LineSegment StartX=15.8 StartY=-10.2 StartZ=0 EndX=15.8 EndY=-15.8 EndZ=0
    g8: LineSegment StartX=15.8 StartY=15.8 StartZ=0 EndX=10.2 EndY=15.8 EndZ=0
    g9: LineSegment StartX=10.2 StartY=15.8 StartZ=0 EndX=10.2 EndY=10.2 EndZ=0
    g10: LineSegment StartX=10.2 StartY=10.2 StartZ=0 EndX=15.8 EndY=10.2 EndZ=0
    g11: LineSegment StartX=15.8 StartY=10.2 StartZ=0 EndX=15.8 EndY=15.8 EndZ=0
    g12: LineSegment StartX=-15.8 StartY=15.8 StartZ=0 EndX=-10.2 EndY=15.8 EndZ=0
    g13: LineSegment StartX=-10.2 StartY=15.8 StartZ=0 EndX=-10.2 EndY=10.2 EndZ=0
    g14: LineSegment StartX=-10.2 StartY=10.2 StartZ=0 EndX=-15.8 EndY=10.2 EndZ=0
    g15: LineSegment StartX=-15.8 StartY=10.2 StartZ=0 EndX=-15.8 EndY=15.8 EndZ=0
  constraints (44):
    c: Coincident(g0,g1)
    c: Coincident(g1,g2)
    c: Coincident(g2,g3)
    c: Coincident(g3,g0)
    c: Horizontal(g0)
    c: Horizontal(g2)
    c: Vertical(g1)
    c: Vertical(g3)
    c: Coincident(g0,g-6)
    c: Coincident(g4,g5)
    c: Coincident(g5,g6)
    c: Coincident(g6,g7)
    c: Coincident(g7,g4)
    c: Horizontal(g4)
    c: Horizontal(g6)
    c: Vertical(g5)
    c: Vertical(g7)
    c: Coincident(g4,g-6)
    c: Coincident(g8,g9)
    c: Coincident(g9,g10)
    c: Coincident(g10,g11)
    c: Coincident(g11,g8)
    c: Horizontal(g8)
    c: Horizontal(g10)
    c: Vertical(g9)
    c: Vertical(g11)
    c: Coincident(g8,g-5)
    c: Coincident(g12,g13)
    c: Coincident(g13,g14)
    c: Coincident(g14,g15)
    c: Coincident(g15,g12)
    c: Horizontal(g12)
    c: Horizontal(g14)
    c: Vertical(g13)
    c: Vertical(g15)
    c: Coincident(g12,g-4)
    c: Equal(g14,g13)
    c: Equal(g9,g10)
    c: Equal(g5,g6)
    c: Equal(g6,g1)
    c: Equal(g1,g2)
    c: Equal(g2,g9)
    c: Equal(g9,g13)
    c: DistanceX(g14,g14) = 5.6
FEATURE [PartDesign::Pad] Pad011  label="Pad_InsertBase"
  BaseFeature = -> Fillet011
  Direction = (0,0,-1)
  Length = 6.7
  Length2 = 10
  Profile = -> Sketch021
  ReferenceAxis = -> Sketch021 [N_Axis]
  Type = 0
  expr: Length = <<params>>.insert_length + 1
FEATURE [Sketcher::SketchObject] Sketch022  label="Sketch_InsertHole"
  ExternalGeometry = -> [Pad011]
  FullyConstrained = true
  MapMode = 5
  Placement = pos=(0,0,-10.7) rot=(1,0,0;3.14159rad)
  Support = -> [Pad011]
  expr: Constraints[14] = (<<params>>.insert_min_wall_thickness + <<params>>.insert_hole_dia) / 2
  expr: Constraints[6] = <<params>>.insert_hole_dia
  sketch-geometry (6):
    g0: Circle CenterX=-13 CenterY=13 CenterZ=0 NormalX=0 NormalY=0 NormalZ=1 AngleXU=0 Radius=2
    g1: Circle CenterX=13 CenterY=13 CenterZ=0 NormalX=0 NormalY=0 NormalZ=1 AngleXU=0 Radius=2
    g2: Circle CenterX=13 CenterY=-13 CenterZ=0 NormalX=0 NormalY=0 NormalZ=1 AngleXU=0 Radius=2
    g3: Circle CenterX=-13 CenterY=-13 CenterZ=0 NormalX=0 NormalY=0 NormalZ=1 AngleXU=0 Radius=2
    g4: LineSegment StartX=-13 StartY=13 StartZ=0 EndX=-13 EndY=10.2 EndZ=0
    g5: LineSegment StartX=-13 StartY=13 StartZ=0 EndX=-10.2 EndY=13 EndZ=0
  constraints (15):
    c: Symmetric(g0,g1,g-2)
    c: Symmetric(g0,g3,g-1)
    c: Symmetric(g2,g1,g-1)
    c: Equal(g0,g1)
    c: Equal(g1,g2)
    c: Equal(g2,g3)
    c: Diameter(g0) = 4
    c: Coincident(g4,g0)
    c: PointOnObject(g4,g-4)
    c: Vertical(g4)
    c: Coincident(g5,g0)
    c: PointOnObject(g5,g-3)
    c: Horizontal(g5)
    c: Equal(g4,g5)
    c: DistanceY(g4,g4) = 2.8
FEATURE [PartDesign::Pocket] Pocket004  label="Pocket_InsertHole"
  BaseFeature = -> Pad011
  Direction = (0,0,1)
  Length = 6.7
  Length2 = 5
  Profile = -> Sketch022
  ReferenceAxis = -> Sketch022 [N_Axis]
  Type = 0
  expr: Length = <<params>>.insert_length + 1
FEATURE [PartDesign::Body] Body028  label="SocketTop"
  Group = -> [Sketch020,Pad010,Chamfer,Fillet011,Sketch021,Pad011,Sketch022,Pocket004,ShapeBinder018]
  Origin = -> Origin056
  Tip = -> Pocket004
FEATURE [PartDesign::ShapeBinder] ShapeBinder019  label="ShapeBinder_PCBBottomFace"
  Support = -> [Part__Feature166]
  TraceSupport = false
FEATURE [PartDesign::ShapeBinder] ShapeBinder020  label="ShapeBinder_SocketInsertBottom"
  Support = -> [Pocket004]
  TraceSupport = false
FEATURE [Sketcher::SketchObject] Sketch023  label="Sketch_3DPrintLegMount"
  ExternalGeometry = -> [ShapeBinder020]
  FullyConstrained = true
  MapMode = 5
  Support = -> [XY_Plane057,ShapeBinder019]
  sketch-geometry (4):
    g0: LineSegment StartX=-15.8 StartY=-15.8 StartZ=0 EndX=-10.2 EndY=-15.8 EndZ=0
    g1: LineSegment StartX=-10.2 StartY=-15.8 StartZ=0 EndX=-10.2 EndY=-10.2 EndZ=0
    g2: LineSegment StartX=-10.2 StartY=-10.2 StartZ=0 EndX=-15.8 EndY=-10.2 EndZ=0
    g3: LineSegment StartX=-15.8 StartY=-10.2 StartZ=0 EndX=-15.8 EndY=-15.8 EndZ=0
  constraints (10):
    c: Coincident(g0,g1)
    c: Coincident(g1,g2)
    c: Coincident(g2,g3)
    c: Coincident(g3,g0)
    c: Horizontal(g0)
    c: Horizontal(g2)
    c: Vertical(g1)
    c: Vertical(g3)
    c: Coincident(g0,g-3)
    c: Coincident(g-4,g1)
FEATURE [PartDesign::Pad] Pad012  label="Pad_3DPrintLegMount"
  Direction = (0,0,1)
  Length = 10
  Length2 = 10
  Profile = -> Sketch023
  ReferenceAxis = -> Sketch023 [N_Axis]
  Reversed = true
  Type = 0
FEATURE [Sketcher::SketchObject] Sketch024  label="Sketch_3DPrintPressFitPins"
  ExternalGeometry = -> [ShapeBinder019]
  FullyConstrained = true
  MapMode = 5
  Placement = pos=(0,0,-10) rot=(1,0,0;3.14159rad)
  Support = -> [Pad012]
  sketch-geometry (1):
    g0: Circle CenterX=-13 CenterY=13 CenterZ=0 NormalX=0 NormalY=0 NormalZ=1 AngleXU=0 Radius=1.6
  constraints (2):
    c: Coincident(g0,g-3)
    c: Tangent(g0,g-3)
FEATURE [PartDesign::Pad] Pad013  label="Pad_3DPrintPressFitPins"
  BaseFeature = -> Pad012
  Direction = (0,0,-1)
  Length = 1.696
  Length2 = 10
  Profile = -> Sketch024
  ReferenceAxis = -> Sketch024 [N_Axis]
  Type = 0
  expr: Length = <<params>>.pcb_thickness * 1.06
FEATURE [PartDesign::Body] Body029  label="3DPrintStand"
  Group = -> [ShapeBinder019,Sketch023,ShapeBinder020,Pad012,Sketch024,Pad013]
  Origin = -> Origin057
  Placement = pos=(0,0,-10.7) rot=(0,0,1;0rad)
  Tip = -> Pad013
  expr: .Placement.Base.z = -(<<params>>.insert_length + 1 + 4)
FEATURE [PartDesign::FeatureBase] Clone015
  BaseFeature = -> Body029
  Placement = pos=(0,0,-10.7) rot=(0,0,1;0rad)
FEATURE [PartDesign::Body] Body030  label="3DPrintStand_2"
  Group = -> [Clone015]
  Origin = -> Origin058
  Placement = pos=(0,0,0) rot=(0,0,1;3.14159rad)
  Tip = -> Clone015
FEATURE [App::Part] Part006  label="KeyboardSocket"
  Group = -> [Body028,Body029,Body030]
  Origin = -> Origin055
  Placement = pos=(0,0,13) rot=(0,0,1;0rad)
FEATURE [Mesh::Feature] M3_Standard
  Placement = pos=(13,13,2.3) rot=(0,0,1;0rad)
FEATURE [Mesh::Feature] M3_Standard001
  Placement = pos=(-13,13,2.3) rot=(0,0,1;0rad)
FEATURE [Mesh::Feature] M3_Standard002
  Placement = pos=(13,-13,2.3) rot=(0,0,1;0rad)
FEATURE [Mesh::Feature] M3_Standard003
  Placement = pos=(-13,-13,2.3) rot=(0,0,1;0rad)
FEATURE [App::DocumentObjectGroup] Group  label="Fasteners"
  Group = -> [Screw,Washer,Nut,Screw001,Washer001,Nut001,M3_Standard,M3_Standard001,M3_Standard002,M3_Standard003]
FEATURE [App::Part] Part002  label="Stick"
  Group = -> [Body003]
  Origin = -> Origin015
FEATURE [PartDesign::Body] Body003  label="MatingCross"
  Group = -> [Sketch007,Binder002,Pad003,ShapeBinder004,Sketch008,Revolution002]
  Origin = -> Origin016
  Tip = -> Revolution002
FEATURE [Sketcher::SketchObject] Sketch007  label="Sketch_MatingCross"
  ExternalGeometry = -> [Binder002]
  FullyConstrained = true
  Placement = pos=(-1.7487e-11,-1.0449e-11,3.5) rot=(0,0,1;0rad)
  Support = -> [Body003,Binder002]
  expr: Constraints[31] = <<params>>.stick_fit_tolerance
  expr: Constraints[32] = <<params>>.stick_fit_tolerance
  sketch-geometry (12):
    g0: LineSegment StartX=3.75 StartY=1.5 StartZ=0 EndX=3.75 EndY=-1.5 EndZ=0
    g1: LineSegment StartX=-3.75 StartY=-1.5 StartZ=0 EndX=-3.75 EndY=1.5 EndZ=0
    g2: LineSegment StartX=-1.5 StartY=3.75 StartZ=0 EndX=1.5 EndY=3.75 EndZ=0
    g3: LineSegment StartX=1.5 StartY=-3.75 StartZ=0 EndX=-1.5 EndY=-3.75 EndZ=0
    g4: LineSegment StartX=-3.75 StartY=1.5 StartZ=0 EndX=-1.5 EndY=1.5 EndZ=0
    g5: LineSegment StartX=-1.5 StartY=1.5 StartZ=0 EndX=-1.5 EndY=3.75 EndZ=0
    g6: LineSegment StartX=-1.5 StartY=-1.5 StartZ=0 EndX=-3.75 EndY=-1.5 EndZ=0
    g7: LineSegment StartX=-1.5 StartY=-3.75 StartZ=0 EndX=-1.5 EndY=-1.5 EndZ=0
    g8: LineSegment StartX=1.5 StartY=-1.5 StartZ=0 EndX=1.5 EndY=-3.75 EndZ=0
    g9: LineSegment StartX=3.75 StartY=-1.5 StartZ=0 EndX=1.5 EndY=-1.5 EndZ=0
    g10: LineSegment StartX=1.5 StartY=3.75 StartZ=0 EndX=1.5 EndY=1.5 EndZ=0
    g11: LineSegment StartX=1.5 StartY=1.5 StartZ=0 EndX=3.75 EndY=1.5 EndZ=0
  constraints (33):
    c: Coincident(g11,g0)
    c: Coincident(g0,g9)
    c: Coincident(g6,g1)
    c: Coincident(g1,g4)
    c: Vertical(g0)
    c: Vertical(g1)
    c: Coincident(g2,g10)
    c: Coincident(g8,g3)
    c: Coincident(g3,g7)
    c: Coincident(g5,g2)
    c: Horizontal(g2)
    c: Horizontal(g3)
    c: Horizontal(g4)
    c: Vertical(g5)
    c: Horizontal(g6)
    c: Vertical(g7)
    c: Vertical(g8)
    c: Horizontal(g9)
    c: Vertical(g10)
    c: Horizontal(g11)
    c: Coincident(g6,g7)
    c: Coincident(g5,g4)
    c: Coincident(g11,g10)
    c: Coincident(g8,g9)
    c: Symmetric(g10,g4,g-2)
    c: Symmetric(g8,g6,g-2)
    c: Symmetric(g10,g8,g-1)
    c: Equal(g6,g9)
    c: Equal(g11,g10)
    c: Equal(g5,g7)
    c: Equal(g3,g1)
    c: DistanceY(g1,g-4) = 0
    c: DistanceX(g-4,g1) = 0
FEATURE [PartDesign::Pad] Pad003  label="Pad_MatingExtrusion"
  Direction = (0,0,1)
  Length = 13
  Length2 = 10
  Placement = pos=(-1.7487e-11,-1.0449e-11,3.5) rot=(0,0,1;0rad)
  Profile = -> Sketch007
  ReferenceAxis = -> Sketch007 [N_Axis]
  Type = 0
  expr: Length = <<params>>.mating_cross_slot_depth + <<params>>.stick_extrusion_height
FEATURE [PartDesign::ShapeBinder] ShapeBinder004  label="ShapeBinder_MatingExtrusion_Top"
  Placement = pos=(0,0,13) rot=(0,0,1;0rad)
  Support = -> [Pad003]
  TraceSupport = false
FEATURE [Sketcher::SketchObject] Sketch008  label="Sketch_Cap"
  AttachmentOffset = pos=(0,0,0) rot=(1,0,0;1.5708rad)
  FullyConstrained = false
  MapMode = 5
  Placement = pos=(0,0,16.5) rot=(1,0,0;1.5708rad)
  Support = -> [ShapeBinder004]
  expr: Constraints[32] = 10
  expr: Constraints[39] = <<params>>.stick_cap_height
  sketch-geometry (20):
    g0: LineSegment StartX=0 StartY=0 StartZ=0 EndX=-10 EndY=0 EndZ=0
    g1: LineSegment StartX=-10 StartY=0 StartZ=0 EndX=-10 EndY=1.96616 EndZ=0
    g2: LineSegment StartX=-10 StartY=1.96616 StartZ=0 EndX=0 EndY=1.96616 EndZ=0
    g3-g6: Circle x4 (B-spline internal-alignment scaffolding for g7; pole/knot coordinates omitted)
    g7: BSplineCurve PolesCount=4 KnotsCount=2 Degree=3 IsPeriodic=0
    g8: GeomPoint X=-10 Y=1.96616 Z=0
    g9: GeomPoint X=-10 Y=3.96616 Z=0
    g10: Circle CenterX=-10 CenterY=3.96616 CenterZ=0 NormalX=0 NormalY=0 NormalZ=1 AngleXU=0 Radius=1
    g11: Circle CenterX=-8.28547 CenterY=4.98296 CenterZ=0 NormalX=0 NormalY=0 NormalZ=1 AngleXU=0 Radius=1
    g12: Circle CenterX=0 CenterY=5 CenterZ=0 NormalX=0 NormalY=0 NormalZ=1 AngleXU=0 Radius=1
    g13: BSplineCurve PolesCount=3 KnotsCount=2 Degree=2 IsPeriodic=0
    g14: GeomPoint X=-10 Y=3.96616 Z=0
    g15: GeomPoint X=0 Y=5 Z=0
    g16: LineSegment StartX=0 StartY=1.96616 StartZ=0 EndX=0 EndY=5 EndZ=0
    g17: LineSegment StartX=-10 StartY=2.96616 StartZ=0 EndX=-10 EndY=3.96616 EndZ=0
    g18: LineSegment StartX=-10 StartY=2.96616 StartZ=0 EndX=-10 EndY=1.96616 EndZ=0
    g19: LineSegment StartX=0 StartY=1.96616 StartZ=0 EndX=0 EndY=0 EndZ=0
  constraints (40):
    c: Coincident(g0,g1)
    c: Coincident(g1,g2)
    c: Horizontal(g0)
    c: Horizontal(g2)
    c: Vertical(g1)
    c: Coincident(g0,g-1)
    c: Weight(g3) = 1
    c: Coincident(g7,g1)
    c: Equal(g3,g4)
    c: PointOnObject(g4,g3)
    c: Equal(g3,g5)
    c: PointOnObject(g5,g4)
    c: Equal(g3,g6)
    c: PointOnObject(g7,g4)
    c: InternalAlignment(g3-g6 -> g7) x4
    c: InternalAlignment(g8,g7)
    c: InternalAlignment(g9,g7)
    c: Weight(g10) = 1
    c: Coincident(g13,g7)
    c: Equal(g10,g11)
    c: Equal(g10,g12)
    c: PointOnObject(g13,g-2)
    c: InternalAlignment(g10,g13)
    c: InternalAlignment(g11,g13)
    c: InternalAlignment(g12,g13)
    c: InternalAlignment(g14,g13)
    c: InternalAlignment(g15,g13)
    c: Coincident(g16,g2)
    c: Coincident(g16,g13)
    c: DistanceX(g0,g0) = 10
    c: Vertical(g1,g4)
    c: Coincident(g17,g4)
    c: Coincident(g17,g7)
    c: Vertical(g17)
    c: Coincident(g18,g4)
    c: Coincident(g18,g1)
    c: DistanceY(g0,g13) = 5
    c: PointOnObject(g16,g-2)
    c: Coincident(g19,g16)
    c: Coincident(g19,g0)
FEATURE [PartDesign::Revolution] Revolution002  label="Revolution_Cap"
  Angle = 360
  Axis = (0,0,1)
  Base = (0,0,16.5)
  BaseFeature = -> Pad003
  Placement = pos=(-1.7487e-11,-1.0449e-11,3.5) rot=(0,0,1;0rad)
  Profile = -> Sketch008
  ReferenceAxis = -> Sketch008 [V_Axis]
FEATURE [App::Part] Part005  label="wholeshebang"
  Group = -> [Body020]
  Origin = -> Origin046
FEATURE [PartDesign::Body] Body020  label="stick"
  Group = -> [Clone007,Boolean002,Boolean003,Boolean004]
  Origin = -> Origin047
  Placement = pos=(0,0,-6.3) rot=(0,0,1;0rad)
  Tip = -> Boolean004
FEATURE [PartDesign::FeatureBase] Clone007
  BaseFeature = -> Body003
FEATURE [PartDesign::Boolean] Boolean002
  BaseFeature = -> Clone007
  Group = -> [Body026]
  Type = 0
FEATURE [PartDesign::Boolean] Boolean003
  BaseFeature = -> Boolean002
  Group = -> [Body023]
  Type = 0
FEATURE [PartDesign::Boolean] Boolean004
  BaseFeature = -> Boolean003
  Group = -> [Body027]
  Type = 0
